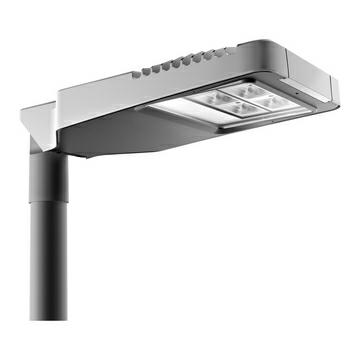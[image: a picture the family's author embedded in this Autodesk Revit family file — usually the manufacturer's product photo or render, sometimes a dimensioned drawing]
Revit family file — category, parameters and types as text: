
# Revit family: Lighting-StreetLighting-GEWISS-ROAD[5]MEDIUM-LED_OPTIC_WIDE_CLI
name_source: partatom
category: Apparecchi per illuminazione
units: mm (PartAtom-declared; Revit-internal decimal feet)

## family parameters
Basato su piano di lavoro = No
Condiviso = No
Punto di calcolo locali = No
Quota connettore circolare = Usa diametro
Sempre verticale = Sì
Sorgente d'illuminazione = No
Taglio con vuoti quando caricato = No
Tipo di parte = Normale

## types (49) — shared parameters
Applicazione = External
Catalogue = LIGHTING
IDF = 8ec06289-ca8c-48b1-8ae5-436b6d1e9ba1
IDT = c439c4f296dc4bdaaede42b4d003d5bb
IP degree = IP66
Immagine tipo = GWR5276M.jpg
Insulation class = I
Lampada = LED
Produttore = GEWISS S.p.A.
SEO = Street lighting
Shock resistance = IK08
Technical sheet = https://www.gewiss.com
URL = https://www.gewiss.com
Version file RFA = 20.11
Warranty = 5 years

## per-type parameters (varying)
- GWR5715M - ROAD5 MEDI WIDE 5M 4000K ,085A CL1 1-10V: Catalogue Range=ROAD [5]; Colour temperature=4000 K (CRI 70); Colour temperature:=4000 K (CRI 70); Descrizione=ROAD 5 MED.DIM.5M 4000K 0,85A O.W CL.I; EAN code=8011564873155; Electrocod=244C; LED LifeTime (L80B05)=120000H; LED current.=0,85A; Lamp-=LED; Lumen output (lm)=17090; Maximum surface exposed to the wind=0,19M2; Minimum distance from the illuminated object=1M; Modello=GWR5715M; No. Chorus modules=5 (5x3 LED); Nominal flux (lm)=21230; Number of modules=5 (5x3 LED); Operating temperature:=-25 +40 °C; Optic=W - ULOR: 0%; Overvoltage resistance=12 KV (Common and dfferential mode); Pilot current=0,85A; Power supply operation=Dimmable; System power=159W; Tilt adjustable=-20° ÷ +10° side bracket - -10° ÷ +20° pole head; Tipo alimentatore=Constant Current Driver Led; Tipologia=Dimmable; Voltage-=220/240 V - 50/60 Hz - Dimmable 1-10 V; Weight (kg)=8,8; Weight (kg):=8,8; Working temperature=-25 +40 °C
- GWR5775 - ROAD 5 MED.S.AL.5M 4000K 700mA O.W CL.I: Catalogue Range=ROAD [5]; Colour temperature=4000 K (CRI 70); Colour temperature:=4000 K (CRI 70); Descrizione=ROAD 5 MED.S.AL.5M 4000K 700mA O.W CL.I; EAN code=8011564873421; Electrocod=244C; LED LifeTime (L80B05)=77000H; LED current.=0,7A; Lamp-=LED; Lumen output (lm)=13100; Maximum surface exposed to the wind=0,19M2; Minimum distance from the illuminated object=1M; Modello=GWR5775; No. Chorus modules=5 (5x3 LED); Nominal flux (lm)=15600; Number of modules=5 (5x3 LED); Operating temperature:=-25 +50 °C; Optic=W - ULOR: 0%; Overvoltage resistance=12 KV (Common and dfferential mode); Pilot current=0,7A; System power=132W; Tilt adjustable=-20° ÷ +10° side bracket - -10° ÷ +20° pole head; Tipo alimentatore=Constant Current Driver Led; Tipologia=Stand alone; Voltage-=220/240 V - 50/60 Hz - Stand alone; Weight (kg)=8,8; Weight (kg):=8,8; Working temperature=-25 +50 °C
- GWR5773 - ROAD5 MEDI WIDE 3M 4000K 0,7A CL1: Catalogue Range=ROAD [5]; Colour temperature=4000 K (CRI 70); Colour temperature:=4000 K (CRI 70); Descrizione=ROAD 5 MED.S.AL.3M 4000K 700mA O.W CL.I; EAN code=8011564873360; Electrocod=244C; LED LifeTime (L80B05)=77000H; LED current.=0,7A; Lamp-=LED; Lumen output (lm)=7860; Maximum surface exposed to the wind=0,19M2; Minimum distance from the illuminated object=1M; Modello=GWR5773; No. Chorus modules=3 (3x3 LED); Nominal flux (lm)=9360; Number of modules=3 (3x3 LED); Operating temperature:=-25 +50 °C; Optic=W - ULOR: 0%; Overvoltage resistance=12 KV (Common and dfferential mode); Pilot current=0,7A; System power=79W; Tilt adjustable=-20° ÷ +10° side bracket - -10° ÷ +20° pole head; Tipo alimentatore=Constant Current Driver Led; Tipologia=Stand alone; Voltage-=220/240 V - 50/60 Hz - Stand alone; Weight (kg)=8; Weight (kg):=8; Working temperature=-25 +50 °C
- GWR5714M30K - ROAD5 MEDI WIDE 4M 3000K 1,0A CL1 1-10V: Body=Die-cast aluminium -; Catalogue Range=ROAD [5]; Classification:=-; Color Rendering Index=CRI-70; Colore=Graphite grey; Colour :=Powder coating; Colour temperature=3000K; Colour temperature:=3000 K (CRI>80); Context=Street and parking lighting; Control System=Dimmable 1-10 V; DIN 18032-3 certification=-; Descrizione=GWR5714M30K - ROAD5 MEDI WIDE 4M 3000K 1,0A CL1 1-10V; Device with reduced surface temperature=-; Driver=Included; Driver Box=Built-in; Efficiency (lm/W)=97; Electrocod=244C; Eletrical and lighting features=-; External screw=Stainless steel; Fixing=Pole Head - Outreach; Gasket=Anti-aging silicone; General information=-; Glow Wire Test :=-; IPEA=ROAD = B // LARGE AREAS = A ++ // CYCLOPEDONALS = B // GREEN AREAS = B // HISTORICAL CENTER = A3 +; Installationa and maintenance=-; LED Life Time (L80B05)=120000H; LED Maintenance=Not available; LED current.=1A; Lamp-=LED; Lifetime=L90B10 (Tq+25°C) = 100.000 h - L90B10 (Tq+40°C) = 50.000 h; Locking Hook=Integrated front handle; Lumen output (lm)=14800; Luminaire=LED Road Equipment; Materials=-; Maximum surface exposed to the wind=0,19M2; Maximum surface exposed to the wind :=0.19 m2; Minimum distance from the illuminated object=1M; Modello=GWR5714M30K; Mouting and installation=Pole Head - Outreach; Nominal flux (lm)=16560; Number of modules=4 (4x3 LED); Operating temperature :=-25 +40 °C; Operating temperature:=-25 +40 °C; Optic=WIDE; Optic :=Metallized polycarbonate reflector; Optic Maintenance=Not available; Optic and illuminating features=-; Overvoltage protection=DM 10KV / CM 10KV; Overvoltage resistance :=Common and dfferential mode: 10KV; Photobiological Risk Class=RG0; Power supply operation=Dimmable; Rated frequency (Hz)=50 / 60; Shield type=4mm thick flat tempered glass; Standard Deviation Colour Matching=SDCM = 5; Standard-=EN 60598-2-3, EN 60598-1 IEC/TR 62778; Standards and approvals=-; Stocking temperature=-; Supply voltage=220 - 240 V; System power=113W; System power :=153 W @ 1A; Tilt adjustable=-20° ÷ +10° side bracket - -10° ÷ +20° pole head; Tilt-=-20° ÷ +10° side bracket - -10° ÷ +20° pole head; Tipo alimentatore=Constant Current Driver Led; Tipologia=Dimmable; Type of light source=LED - Not replaceable; Unified Glare Rating=G*3 - ULOR = 0; Unique digital code (Datamatrix)=Currently not present; Voltage-=220/240 V - 50/60 Hz - Dimmable 1-10 V; Weight (kg):=8,4; Wiring=Isolating switch
- GWR5774B30K - ROAD5 MEDI WIDE 4M 3000K 0,7A CL1 BIREG: Body=Die-cast aluminium -; Catalogue Range=ROAD [5]; Classification:=-; Color Rendering Index=CRI-70; Colore=Graphite grey; Colour :=Powder coating; Colour temperature=3000K; Colour temperature:=3000 K (CRI>80); Context=Street and parking lighting; Control System=Bi-power with self-learning; DIN 18032-3 certification=-; Descrizione=GWR5774B30K - ROAD5 MEDI WIDE 4M 3000K 0,7A CL1 BIREG; Device with reduced surface temperature=-; Driver=Included; Driver Box=Built-in; Efficiency (lm/W)=102; Electrocod=244C; Eletrical and lighting features=-; External screw=Stainless steel; Fixing=Pole Head - Outreach; Gasket=Anti-aging silicone; General information=-; Glow Wire Test :=-; IPEA=ROAD = A + // LARGE AREAS = A3 + // CYCLOPEDONALS = A // GREEN AREAS = A // HISTORICAL CENTER = A4 +; Installationa and maintenance=-; LED Life Time (L80B05)=77000H; LED Maintenance=Not available; LED current.=0,7A; Lamp-=LED; Lifetime=L90B10 (Tq+25°C) = 100.000 h - L90B10 (Tq+50°C) = 50.000 h; Locking Hook=Integrated front handle; Lumen output (lm)=11000; Luminaire=LED Road Equipment; Materials=-; Maximum surface exposed to the wind=0,19M2; Maximum surface exposed to the wind :=0.19 m2; Minimum distance from the illuminated object=1M; Modello=GWR5774B30K; Mouting and installation=Pole Head - Outreach; Nominal flux (lm)=10800; Number of modules=4 (4x3 LED); Operating temperature :=-25 +50 °C; Operating temperature:=-25 +50 °C; Optic=WIDE; Optic :=Metallized polycarbonate reflector; Optic Maintenance=Not available; Optic and illuminating features=-; Overvoltage protection=DM 10KV / CM 10KV; Overvoltage resistance :=Common and dfferential mode: 10KV; Photobiological Risk Class=RG0; Power supply operation=Bi power; Rated frequency (Hz)=50 / 60; Shield type=4mm thick flat tempered glass; Standard Deviation Colour Matching=SDCM = 5; Standard-=EN 60598-2-3, EN 60598-1 IEC/TR 62778; Standards and approvals=-; Stocking temperature=-; Supply voltage=220 - 240 V; System power=108W; System power :=108 W @ 0.7A; Tilt adjustable=-20° ÷ +10° side bracket - -10° ÷ +20° pole head; Tilt-=-20° ÷ +10° side bracket - -10° ÷ +20° pole head; Tipo alimentatore=Constant Current Driver Led; Tipologia=Bi power; Type of light source=LED - Not replaceable; Unified Glare Rating=G*3 - ULOR = 0; Unique digital code (Datamatrix)=Currently not present; Voltage-=220/240 V - 50/60 Hz - Bi-power with self-learning; Weight (kg):=8,4; Wiring=Isolating switch
- GWR571630K - ROAD5 MEDI WIDE 6M 3000K 0,85A CL1: Body=Die-cast aluminium -; Catalogue Range=ROAD [5]; Classification:=-; Color Rendering Index=CRI-70; Colore=Graphite grey; Colour :=Powder coating; Colour temperature=3000K; Colour temperature:=3000 K (CRI>80); Context=Street and parking lighting; Control System=Stand alone; DIN 18032-3 certification=-; Descrizione=GWR571630K - ROAD5 MEDI WIDE 6M 3000K 0,85A CL1; Device with reduced surface temperature=-; Driver=Included; Driver Box=Built-in; Efficiency (lm/W)=105; Electrocod=244C; Eletrical and lighting features=-; External screw=Stainless steel; Fixing=Pole Head - Outreach; Gasket=Anti-aging silicone; General information=-; Glow Wire Test :=-; IPEA=ROAD = B // LARGE AREAS = A ++ // CYCLOPEDONALS = A // GREEN AREAS = A // HISTORICAL CENTER = A3 +; Installationa and maintenance=-; LED Life Time (L80B05)=120000H; LED Maintenance=Not available; LED current.=0,849999999999999A; Lamp-=LED; Lifetime=L90B10 (Tq+25°C) = 100.000 h - L90B10 (Tq+40°C) = 50.000 h; Locking Hook=Integrated front handle; Lumen output (lm)=19400; Luminaire=LED Road Equipment; Materials=-; Maximum surface exposed to the wind=0,19M2; Maximum surface exposed to the wind :=0.19 m2; Minimum distance from the illuminated object=1M; Modello=GWR571630K; Mouting and installation=Pole Head - Outreach; Nominal flux (lm)=21114; Number of modules=6 (6x3 LED); Operating temperature :=-25 +40 °C; Operating temperature:=-25 +40 °C; Optic=WIDE; Optic :=Metallized polycarbonate reflector; Optic Maintenance=Not available; Optic and illuminating features=-; Overvoltage protection=DM 10KV / CM 10KV; Overvoltage resistance :=Common and dfferential mode: 10KV; Photobiological Risk Class=RG0; Rated frequency (Hz)=50 / 60; Shield type=4mm thick flat tempered glass; Standard Deviation Colour Matching=SDCM = 5; Standard-=EN 60598-2-3, EN 60598-1 IEC/TR 62778; Standards and approvals=-; Stocking temperature=-; Supply voltage=220 - 240 V; System power=185W; System power :=185 W @ 0.85A; Tilt adjustable=-20° ÷ +10° side bracket - -10° ÷ +20° pole head; Tilt-=-20° ÷ +10° side bracket - -10° ÷ +20° pole head; Tipo alimentatore=Constant Current Driver Led; Tipologia=Stand alone; Type of light source=LED - Not replaceable; Unified Glare Rating=G*3 - ULOR = 0; Unique digital code (Datamatrix)=Currently not present; Voltage-=220/240 V - 50/60 Hz - Stand alone; Weight (kg):=9,09999999999999; Wiring=Isolating switch
- GWR5776 - ROAD5 MEDI WIDE 6M 4000K 0,7A CL1: Catalogue Range=ROAD [5]; Colour temperature=4000 K (CRI 70); Colour temperature:=4000 K (CRI 70); Descrizione=ROAD 5 MED.S.AL.6M 4000K 700mA O.W CL.I; EAN code=8011564873452; Electrocod=244C; LED LifeTime (L80B05)=77000H; LED current.=0,7A; Lamp-=LED; Lumen output (lm)=15730; Maximum surface exposed to the wind=0,19M2; Minimum distance from the illuminated object=1M; Modello=GWR5776; No. Chorus modules=6 (6x3 LED); Nominal flux (lm)=18720; Number of modules=6 (6x3 LED); Operating temperature:=-25 +50 °C; Optic=W - ULOR: 0%; Overvoltage resistance=12 KV (Common and dfferential mode); Pilot current=0,7A; System power=159W; Tilt adjustable=-20° ÷ +10° side bracket - -10° ÷ +20° pole head; Tipo alimentatore=Constant Current Driver Led; Tipologia=Stand alone; Voltage-=220/240 V - 50/60 Hz - Stand alone; Weight (kg)=9.1; Weight (kg):=9,1; Working temperature=-25 +50 °C
- GWR5776B30K - ROAD5 MEDI WIDE 6M 3000K 0,7A CL1 BIREG: Body=Die-cast aluminium -; Catalogue Range=ROAD [5]; Classification:=-; Color Rendering Index=CRI-70; Colore=Graphite grey; Colour :=Powder coating; Colour temperature=3000K; Colour temperature:=3000 K (CRI>80); Context=Street and parking lighting; Control System=Bi-power with self-learning; DIN 18032-3 certification=-; Descrizione=GWR5776B30K - ROAD5 MEDI WIDE 6M 3000K 0,7A CL1 BIREG; Device with reduced surface temperature=-; Driver=Included; Driver Box=Built-in; Efficiency (lm/W)=102; Electrocod=244C; Eletrical and lighting features=-; External screw=Stainless steel; Fixing=Pole Head - Outreach; Gasket=Anti-aging silicone; General information=-; Glow Wire Test :=-; IPEA=ROAD = A // LARGE AREAS = A3 + // CYCLOPEDONALS = A // GREEN AREAS = A // HISTORICAL CENTER = A4 +; Installationa and maintenance=-; LED Life Time (L80B05)=77000H; LED Maintenance=Not available; LED current.=0,7A; Lamp-=LED; Lifetime=L90B10 (Tq+25°C) = 100.000 h - L90B10 (Tq+50°C) = 50.000 h; Locking Hook=Integrated front handle; Lumen output (lm)=16500; Luminaire=LED Road Equipment; Materials=-; Maximum surface exposed to the wind=0,19M2; Maximum surface exposed to the wind :=0.19 m2; Minimum distance from the illuminated object=1M; Modello=GWR5776B30K; Mouting and installation=Pole Head - Outreach; Nominal flux (lm)=16200; Number of modules=6 (6x3 LED); Operating temperature :=-25 +50 °C; Operating temperature:=-25 +50 °C; Optic=WIDE; Optic :=Metallized polycarbonate reflector; Optic Maintenance=Not available; Optic and illuminating features=-; Overvoltage protection=DM 10KV / CM 10KV; Overvoltage resistance :=Common and dfferential mode: 10KV; Photobiological Risk Class=RG0; Power supply operation=Bi power; Rated frequency (Hz)=50 / 60; Shield type=4mm thick flat tempered glass; Standard Deviation Colour Matching=SDCM = 5; Standard-=EN 60598-2-3, EN 60598-1 IEC/TR 62778; Standards and approvals=-; Stocking temperature=-; Supply voltage=220 - 240 V; System power=161W; System power :=161 W @ 0.7A; Tilt adjustable=-20° ÷ +10° side bracket - -10° ÷ +20° pole head; Tilt-=-20° ÷ +10° side bracket - -10° ÷ +20° pole head; Tipo alimentatore=Constant Current Driver Led; Tipologia=Bi power; Type of light source=LED - Not replaceable; Unified Glare Rating=G*3 - ULOR = 0; Unique digital code (Datamatrix)=Currently not present; Voltage-=220/240 V - 50/60 Hz - Bi-power with self-learning; Weight (kg):=9,09999999999999; Wiring=Isolating switch
- GWR5776M - ROAD5 MEDI WIDE 6M 4000K 0,7A CL1 1-10V: Catalogue Range=ROAD [5]; Colour temperature=4000 K (CRI 70); Colour temperature:=4000 K (CRI 70); Descrizione=ROAD 5 MED.DIM.6M 4000K 700mA O.W CL.I; EAN code=8011564873476; Electrocod=244C; LED LifeTime (L80B05)=77000H; LED current.=0,7A; Lamp-=LED; Lumen output (lm)=15730; Maximum surface exposed to the wind=0,19M2; Minimum distance from the illuminated object=1M; Modello=GWR5776M; No. Chorus modules=6 (6x3 LED); Nominal flux (lm)=18720; Number of modules=6 (6x3 LED); Operating temperature:=-25 +50 °C; Optic=W - ULOR: 0%; Overvoltage resistance=12 KV (Common and dfferential mode); Pilot current=0,7A; Power supply operation=Dimmable; System power=159W; Tilt adjustable=-20° ÷ +10° side bracket - -10° ÷ +20° pole head; Tipo alimentatore=Constant Current Driver Led; Tipologia=Dimmable; Voltage-=220/240 V - 50/60 Hz - Dimmable 1-10 V; Weight (kg)=9.1; Weight (kg):=9,1; Working temperature=-25 +50 °C
- GWR5775M - ROAD5 MEDI WIDE 5M 4000K 0,7A CL1 1-10V: Catalogue Range=ROAD [5]; Colour temperature=4000 K (CRI 70); Colour temperature:=4000 K (CRI 70); Descrizione=ROAD 5 MED.DIM.5M 4000K 700mA O.W CL.I; EAN code=8011564873445; Electrocod=244C; LED LifeTime (L80B05)=77000H; LED current.=0,7A; Lamp-=LED; Lumen output (lm)=13100; Maximum surface exposed to the wind=0,19M2; Minimum distance from the illuminated object=1M; Modello=GWR5775M; No. Chorus modules=5 (5x3 LED); Nominal flux (lm)=15600; Number of modules=5 (5x3 LED); Operating temperature:=-25 +50 °C; Optic=W - ULOR: 0%; Overvoltage resistance=12 KV (Common and dfferential mode); Pilot current=0,7A; Power supply operation=Dimmable; System power=132W; Tilt adjustable=-20° ÷ +10° side bracket - -10° ÷ +20° pole head; Tipo alimentatore=Constant Current Driver Led; Tipologia=Dimmable; Voltage-=220/240 V - 50/60 Hz - Dimmable 1-10 V; Weight (kg)=8,8; Weight (kg):=8,8; Working temperature=-25 +50 °C
- GWR5773B - ROAD5 MEDI WIDE 3M 4000K 0,7A CL1 BIREG: Catalogue Range=ROAD [5]; Colour temperature=4000 K (CRI 70); Colour temperature:=4000 K (CRI 70); Descrizione=ROAD 5 MED.BI-PO.3M 4000K 700mA O.W CL.I; EAN code=8011564873377; Electrocod=244C; LED LifeTime (L80B05)=77000H; LED current.=0,7A; Lamp-=LED; Lumen output (lm)=7860; Maximum surface exposed to the wind=0,19M2; Minimum distance from the illuminated object=1M; Modello=GWR5773B; No. Chorus modules=3 (3x3 LED); Nominal flux (lm)=9360; Number of modules=3 (3x3 LED); Operating temperature:=-25 +50 °C; Optic=W - ULOR: 0%; Overvoltage resistance=12 KV (Common and dfferential mode); Pilot current=0,7A; Power supply operation=Bi power; System power=81W; Tilt adjustable=-20° ÷ +10° side bracket - -10° ÷ +20° pole head; Tipo alimentatore=Constant Current Driver Led; Tipologia=Bi power; Voltage-=220/240 V - 50/60 Hz - Bi-power with self-learning; Weight (kg)=8; Weight (kg):=8; Working temperature=-25 +50 °C
- GWR5713M - ROAD5 MEDI WIDE 3M 4000K 1,0A CL1 1-10V: Catalogue Range=ROAD [5]; Colour temperature=4000 K (CRI 70); Colour temperature:=4000 K (CRI 70); Descrizione=ROAD 5 MED.DIM.3M 4000K 1A O.W CL.I; EAN code=8011564873094; Electrocod=244C; LED LifeTime (L80B05)=120000H; LED current.=1A; Lamp-=LED; Lumen output (lm)=11520; Maximum surface exposed to the wind=0,19M2; Minimum distance from the illuminated object=1M; Modello=GWR5713M; No. Chorus modules=3 (3x3 LED); Nominal flux (lm)=14310; Number of modules=3 (3x3 LED); Operating temperature:=-25 +40 °C; Optic=W - ULOR: 0%; Overvoltage resistance=12 KV (Common and dfferential mode); Pilot current=1A; Power supply operation=Dimmable; System power=113W; Tilt adjustable=-20° ÷ +10° side bracket - -10° ÷ +20° pole head; Tipo alimentatore=Constant Current Driver Led; Tipologia=Dimmable; Voltage-=220/240 V - 50/60 Hz - Dimmable 1-10 V; Weight (kg)=8; Weight (kg):=8; Working temperature=-25 +40 °C
- GWR5716B - ROAD5 MEDI WIDE 6M 4000K 0,85A CL1 BIREG: Catalogue Range=ROAD [5]; Colour temperature=4000 K (CRI 70); Colour temperature:=4000 K (CRI 70); Descrizione=ROAD5 MED.BI-POW.6M 4000K 0,85A O.W CL.I; EAN code=8011564873179; Electrocod=244C; LED LifeTime (L80B05)=120000H; LED current.=0,85A; Lamp-=LED; Lumen output (lm)=19580; Maximum surface exposed to the wind=0,19M2; Minimum distance from the illuminated object=1M; Modello=GWR5716B; No. Chorus modules=6 (6x3 LED); Nominal flux (lm)=24330; Number of modules=6 (6x3 LED); Operating temperature:=-25 +40 °C; Optic=W - ULOR: 0%; Overvoltage resistance=12 KV (Common and dfferential mode); Pilot current=0,85A; Power supply operation=Bi power; System power=187W; Tilt adjustable=-20° ÷ +10° side bracket - -10° ÷ +20° pole head; Tipo alimentatore=Constant Current Driver Led; Tipologia=Bi power; Voltage-=220/240 V - 50/60 Hz - Bi-power with self-learning; Weight (kg)=9.1; Weight (kg):=9,1; Working temperature=-25 +40 °C
- GWR5714 - ROAD 5 MED.S.AL.4M 4000K 1A O.W CL.I: Catalogue Range=ROAD [5]; Colour temperature=4000 K (CRI 70); Colour temperature:=4000 K (CRI 70); Descrizione=ROAD 5 MED.S.AL.4M 4000K 1A O.W CL.I; EAN code=8011564873100; Electrocod=244C; LED LifeTime (L80B05)=120000H; LED current.=1A; Lamp-=LED; Lumen output (lm)=15360; Maximum surface exposed to the wind=0,19M2; Minimum distance from the illuminated object=1M; Modello=GWR5714; No. Chorus modules=4 (4x3 LED); Nominal flux (lm)=19080; Number of modules=4 (4x3 LED); Operating temperature:=-25 +40 °C; Optic=W - ULOR: 0%; Overvoltage resistance=12 KV (Common and dfferential mode); Pilot current=1A; System power=151W; Tilt adjustable=-20° ÷ +10° side bracket - -10° ÷ +20° pole head; Tipo alimentatore=Constant Current Driver Led; Tipologia=Stand alone; Voltage-=220/240 V - 50/60 Hz - Stand alone; Weight (kg)=8,4; Weight (kg):=8,4; Working temperature=-25 +40 °C
- GWR5715 - ROAD 5 MED.S.AL.5M 4000K 0,85A O.W CL.I: Catalogue Range=ROAD [5]; Colour temperature=4000 K (CRI 70); Colour temperature:=4000 K (CRI 70); Descrizione=ROAD 5 MED.S.AL.5M 4000K 0,85A O.W CL.I; EAN code=8011564873131; Electrocod=244C; LED LifeTime (L80B05)=120000H; LED current.=0,85A; Lamp-=LED; Lumen output (lm)=17090; Maximum surface exposed to the wind=0,19M2; Minimum distance from the illuminated object=1M; Modello=GWR5715; No. Chorus modules=5 (5x3 LED); Nominal flux (lm)=21230; Number of modules=5 (5x3 LED); Operating temperature:=-25 +40 °C; Optic=W - ULOR: 0%; Overvoltage resistance=12 KV (Common and dfferential mode); Pilot current=0,85A; System power=159W; Tilt adjustable=-20° ÷ +10° side bracket - -10° ÷ +20° pole head; Tipo alimentatore=Constant Current Driver Led; Tipologia=Stand alone; Voltage-=220/240 V - 50/60 Hz - Stand alone; Weight (kg)=8,8; Weight (kg):=8,8; Working temperature=-25 +40 °C
- GWR571330K - ROAD5 MEDI WIDE 3M 3000K 1,0A CL1: Body=Die-cast aluminium -; Catalogue Range=ROAD [5]; Classification:=-; Color Rendering Index=CRI-70; Colore=Graphite grey; Colour :=Powder coating; Colour temperature=3000K; Colour temperature:=3000 K (CRI>80); Context=Street and parking lighting; Control System=Stand alone; DIN 18032-3 certification=-; Descrizione=GWR571330K - ROAD5 MEDI WIDE 3M 3000K 1,0A CL1; Device with reduced surface temperature=-; Driver=Included; Driver Box=Built-in; Efficiency (lm/W)=98; Electrocod=244C; Eletrical and lighting features=-; External screw=Stainless steel; Fixing=Pole Head - Outreach; Gasket=Anti-aging silicone; General information=-; Glow Wire Test :=-; IPEA=ROAD = A // LARGE AREAS = A3 + // CYCLOPEDONALS = A // GREEN AREAS = A // HISTORICAL CENTER = A4 +; Installationa and maintenance=-; LED Life Time (L80B05)=120000H; LED Maintenance=Not available; LED current.=1A; Lamp-=LED; Lifetime=L90B10 (Tq+25°C) = 100.000 h - L90B10 (Tq+40°C) = 75.000 h; Locking Hook=Integrated front handle; Lumen output (lm)=11100; Luminaire=LED Road Equipment; Materials=-; Maximum surface exposed to the wind=0,19M2; Maximum surface exposed to the wind :=0.19 m2; Minimum distance from the illuminated object=1M; Modello=GWR571330K; Mouting and installation=Pole Head - Outreach; Nominal flux (lm)=12420; Number of modules=3 (3x3 LED); Operating temperature :=-25 +40 °C; Operating temperature:=-25 +40 °C; Optic=WIDE; Optic :=Metallized polycarbonate reflector; Optic Maintenance=Not available; Optic and illuminating features=-; Overvoltage protection=DM 10KV / CM 10KV; Overvoltage resistance :=Common and dfferential mode: 10KV; Photobiological Risk Class=RG0; Rated frequency (Hz)=50 / 60; Shield type=4mm thick flat tempered glass; Standard Deviation Colour Matching=SDCM = 5; Standard-=EN 60598-2-3, EN 60598-1 IEC/TR 62778; Standards and approvals=-; Stocking temperature=-; Supply voltage=220 - 240 V; System power=113W; System power :=113 W @ 1A; Tilt adjustable=-20° ÷ +10° side bracket - -10° ÷ +20° pole head; Tilt-=-20° ÷ +10° side bracket - -10° ÷ +20° pole head; Tipo alimentatore=Constant Current Driver Led; Tipologia=Stand alone; Type of light source=LED - Not replaceable; Unified Glare Rating=G*3 - ULOR = 0; Unique digital code (Datamatrix)=Currently not present; Voltage-=220/240 V - 50/60 Hz - Stand alone; Weight (kg):=8; Wiring=Isolating switch
- GWR5713V - ROAD5 MEDI V.WIDE 3M 4000K 1,0A CL1: Body=Die-cast aluminium -; Classification:=-; Color Rendering Index=CRI-70; Colore=Graphite grey; Colour :=Powder coating; Colour temperature=4000K; Context=Street and parking lighting; Control System=DALI; DIN 18032-3 certification=-; Descrizione=GWR5713V - ROAD5 MEDI V.WIDE 3M 4000K 1,0A CL1; Device with reduced surface temperature=-; Driver=Included; Driver Box=Built-in; Efficiency (lm/W)=111; Eletrical and lighting features=-; External screw=Stainless steel; Fixing=Pole Head - Outreach; Gasket=Anti-aging silicone; General information=-; Glow Wire Test :=-; IPEA=ROAD = A ++ // LARGE AREAS = A4 + // CYCLOPEDONALS = A ++ // GREEN AREAS = A ++ // HISTORICAL CENTER = A6 +; Installationa and maintenance=-; LED Maintenance=Not available; Lifetime=L90B10 (Tq+25°C) = 100.000 h - L90B10 (Tq+40°C) = 75.000 h; Locking Hook=Integrated front handle; Lumen output (lm)=12800; Luminaire=LED Road Equipment; Materials=-; Maximum surface exposed to the wind :=0.19 m2; Modello=GWR5713V; Mouting and installation=Pole Head - Outreach; Number of modules=3 (3x3 LED); Operating temperature :=-25 +40 °C; Optic=WIDE; Optic :=Metallized polycarbonate reflector; Optic Maintenance=Not available; Optic and illuminating features=-; Overvoltage protection=DM 10KV / CM 10KV; Photobiological Risk Class=RG0; Rated frequency (Hz)=50 / 60; Shield type=4mm thick flat tempered glass; Standard Deviation Colour Matching=SDCM = 5; Standard-=EN 60598-2-3, EN 60598-1 IEC/TR 62778; Standards and approvals=-; Stocking temperature=-; Supply voltage=220 - 240 V; System power :=115 W @ 1A; Tilt-=-20° ÷ +10° side bracket - -10° ÷ +20° pole head; Type of light source=LED - Not replaceable; Unified Glare Rating=G*3 - ULOR = 0; Unique digital code (Datamatrix)=Currently not present; Weight (kg):=8; Wiring=Isolating switch
- GWR5716M30K - ROAD5 MEDI WIDE 6M 3000K 0,85A CL1 1-10V: Body=Die-cast aluminium -; Catalogue Range=ROAD [5]; Classification:=-; Color Rendering Index=CRI-70; Colore=Graphite grey; Colour :=Powder coating; Colour temperature=3000K; Colour temperature:=3000 K (CRI>80); Context=Street and parking lighting; Control System=Dimmable 1-10 V; DIN 18032-3 certification=-; Descrizione=GWR5716M30K - ROAD5 MEDI WIDE 6M 3000K 0,85A CL1 1-10V; Device with reduced surface temperature=-; Driver=Included; Driver Box=Built-in; Efficiency (lm/W)=104; Electrocod=244C; Eletrical and lighting features=-; External screw=Stainless steel; Fixing=Pole Head - Outreach; Gasket=Anti-aging silicone; General information=-; Glow Wire Test :=-; IPEA=ROAD = B // LARGE AREAS = A ++ // CYCLOPEDONALS = A // GREEN AREAS = A // HISTORICAL CENTER = A3 +; Installationa and maintenance=-; LED Life Time (L80B05)=120000H; LED Maintenance=Not available; LED current.=0,849999999999999A; Lamp-=LED; Lifetime=L90B10 (Tq+25°C) = 100.000 h - L90B10 (Tq+40°C) = 50.000 h; Locking Hook=Integrated front handle; Lumen output (lm)=19400; Luminaire=LED Road Equipment; Materials=-; Maximum surface exposed to the wind=0,19M2; Maximum surface exposed to the wind :=0.19 m2; Minimum distance from the illuminated object=1M; Modello=GWR5716M30K; Mouting and installation=Pole Head - Outreach; Nominal flux (lm)=21114; Number of modules=6 (6x3 LED); Operating temperature :=-25 +40 °C; Operating temperature:=-25 +40 °C; Optic=WIDE; Optic :=Metallized polycarbonate reflector; Optic Maintenance=Not available; Optic and illuminating features=-; Overvoltage protection=DM 10KV / CM 10KV; Overvoltage resistance :=Common and dfferential mode: 10KV; Photobiological Risk Class=RG0; Power supply operation=Dimmable; Rated frequency (Hz)=50 / 60; Shield type=4mm thick flat tempered glass; Standard Deviation Colour Matching=SDCM = 5; Standard-=EN 60598-2-3, EN 60598-1 IEC/TR 62778; Standards and approvals=-; Stocking temperature=-; Supply voltage=220 - 240 V; System power=185W; System power :=187 W @ 0.85A; Tilt adjustable=-20° ÷ +10° side bracket - -10° ÷ +20° pole head; Tilt-=-20° ÷ +10° side bracket - -10° ÷ +20° pole head; Tipo alimentatore=Constant Current Driver Led; Tipologia=Dimmable; Type of light source=LED - Not replaceable; Unified Glare Rating=G*3 - ULOR = 0; Unique digital code (Datamatrix)=Currently not present; Voltage-=220/240 V - 50/60 Hz - Dimmable 1-10 V; Weight (kg):=9,09999999999999; Wiring=Isolating switch
- GWR577630K - ROAD5 MEDI WIDE 6M 3000K 0,7A CL1: Body=Die-cast aluminium -; Catalogue Range=ROAD [5]; Classification:=-; Color Rendering Index=CRI-70; Colore=Graphite grey; Colour :=Powder coating; Colour temperature=3000K; Colour temperature:=3000 K (CRI>80); Context=Street and parking lighting; Control System=Stand alone; DIN 18032-3 certification=-; Descrizione=GWR577630K - ROAD5 MEDI WIDE 6M 3000K 0,7A CL1; Device with reduced surface temperature=-; Driver=Included; Driver Box=Built-in; Efficiency (lm/W)=104; Electrocod=244C; Eletrical and lighting features=-; External screw=Stainless steel; Fixing=Pole Head - Outreach; Gasket=Anti-aging silicone; General information=-; Glow Wire Test :=-; IPEA=ROAD = A // LARGE AREAS = A3 + // CYCLOPEDONALS = A // GREEN AREAS = A // HISTORICAL CENTER = A4 +; Installationa and maintenance=-; LED Life Time (L80B05)=77000H; LED Maintenance=Not available; LED current.=0,7A; Lamp-=LED; Lifetime=L90B10 (Tq+25°C) = 100.000 h - L90B10 (Tq+50°C) = 50.000 h; Locking Hook=Integrated front handle; Lumen output (lm)=16500; Luminaire=LED Road Equipment; Materials=-; Maximum surface exposed to the wind=0,19M2; Maximum surface exposed to the wind :=0.19 m2; Minimum distance from the illuminated object=1M; Modello=GWR577630K; Mouting and installation=Pole Head - Outreach; Nominal flux (lm)=16200; Number of modules=6 (6x3 LED); Operating temperature :=-25 +50 °C; Operating temperature:=-25 +50 °C; Optic=WIDE; Optic :=Metallized polycarbonate reflector; Optic Maintenance=Not available; Optic and illuminating features=-; Overvoltage protection=DM 10KV / CM 10KV; Overvoltage resistance :=Common and dfferential mode: 10KV; Photobiological Risk Class=RG0; Rated frequency (Hz)=50 / 60; Shield type=4mm thick flat tempered glass; Standard Deviation Colour Matching=SDCM = 5; Standard-=EN 60598-2-3, EN 60598-1 IEC/TR 62778; Standards and approvals=-; Stocking temperature=-; Supply voltage=220 - 240 V; System power=159W; System power :=159 W @ 0.7A; Tilt adjustable=-20° ÷ +10° side bracket - -10° ÷ +20° pole head; Tilt-=-20° ÷ +10° side bracket - -10° ÷ +20° pole head; Tipo alimentatore=Constant Current Driver Led; Tipologia=Stand alone; Type of light source=LED - Not replaceable; Unified Glare Rating=G*3 - ULOR = 0; Unique digital code (Datamatrix)=Currently not present; Voltage-=220/240 V - 50/60 Hz - Stand alone; Weight (kg):=9,09999999999999; Wiring=Isolating switch
- GWR571530K - ROAD5 MEDI WIDE 5M 3000K 0,85A CL1: Body=Die-cast aluminium -; Catalogue Range=ROAD [5]; Classification:=-; Color Rendering Index=CRI-70; Colore=Graphite grey; Colour :=Powder coating; Colour temperature=3000K; Colour temperature:=3000 K (CRI>80); Context=Street and parking lighting; Control System=Stand alone; DIN 18032-3 certification=-; Descrizione=GWR571530K - ROAD5 MEDI WIDE 5M 3000K 0,85A CL1; Device with reduced surface temperature=-; Driver=Included; Driver Box=Built-in; Efficiency (lm/W)=102; Electrocod=244C; Eletrical and lighting features=-; External screw=Stainless steel; Fixing=Pole Head - Outreach; Gasket=Anti-aging silicone; General information=-; Glow Wire Test :=-; IPEA=ROAD = A // LARGE AREAS = A3 + // CYCLOPEDONALS = A // GREEN AREAS = A // HISTORICAL CENTER = A4 +; Installationa and maintenance=-; LED Life Time (L80B05)=120000H; LED Maintenance=Not available; LED current.=0,849999999999999A; Lamp-=LED; Lifetime=L90B10 (Tq+25°C) = 100.000 h - L90B10 (Tq+40°C) = 50.000 h; Locking Hook=Integrated front handle; Lumen output (lm)=16200; Luminaire=LED Road Equipment; Materials=-; Maximum surface exposed to the wind=0,19M2; Maximum surface exposed to the wind :=0.19 m2; Minimum distance from the illuminated object=1M; Modello=GWR571530K; Mouting and installation=Pole Head - Outreach; Nominal flux (lm)=18423; Number of modules=5 (5x3 LED); Operating temperature :=-25 +40 °C; Operating temperature:=-25 +40 °C; Optic=WIDE; Optic :=Metallized polycarbonate reflector; Optic Maintenance=Not available; Optic and illuminating features=-; Overvoltage protection=DM 10KV / CM 10KV; Overvoltage resistance :=Common and dfferential mode: 10KV; Photobiological Risk Class=RG0; Rated frequency (Hz)=50 / 60; Shield type=4mm thick flat tempered glass; Standard Deviation Colour Matching=SDCM = 5; Standard-=EN 60598-2-3, EN 60598-1 IEC/TR 62778; Standards and approvals=-; Stocking temperature=-; Supply voltage=220 - 240 V; System power=159W; System power :=159 W @ 0.85A; Tilt adjustable=-20° ÷ +10° side bracket - -10° ÷ +20° pole head; Tilt-=-20° ÷ +10° side bracket - -10° ÷ +20° pole head; Tipo alimentatore=Constant Current Driver Led; Tipologia=Stand alone; Type of light source=LED - Not replaceable; Unified Glare Rating=G*3 - ULOR = 0; Unique digital code (Datamatrix)=Currently not present; Voltage-=220/240 V - 50/60 Hz - Stand alone; Weight (kg):=8,8; Wiring=Isolating switch
- GWR5773M30K - ROAD5 MEDI WIDE 3M 3000K 0,7A CL1 1-10V: Body=Die-cast aluminium -; Catalogue Range=ROAD [5]; Classification:=-; Color Rendering Index=CRI-70; Colore=Graphite grey; Colour :=Powder coating; Colour temperature=3000K; Colour temperature:=3000 K (CRI>80); Context=Street and parking lighting; Control System=Dimmable 1-10 V; DIN 18032-3 certification=-; Descrizione=GWR5773M30K - ROAD5 MEDI WIDE 3M 3000K 0,7A CL1 1-10V; Device with reduced surface temperature=-; Driver=Included; Driver Box=Built-in; Efficiency (lm/W)=102; Electrocod=244C; Eletrical and lighting features=-; External screw=Stainless steel; Fixing=Pole Head - Outreach; Gasket=Anti-aging silicone; General information=-; Glow Wire Test :=-; IPEA=ROAD = A ++ // LARGE AREAS = A3 + // CYCLOPEDONALS = A + // GREEN AREAS = A + // HISTORICAL CENTER = A6 +; Installationa and maintenance=-; LED Life Time (L80B05)=77000H; LED Maintenance=Not available; LED current.=0,7A; Lamp-=LED; Lifetime=L90B10 (Tq+25°C) = 100.000 h - L90B10 (Tq+50°C) = 75.000 h; Locking Hook=Integrated front handle; Lumen output (lm)=8300; Luminaire=LED Road Equipment; Materials=-; Maximum surface exposed to the wind=0,19M2; Maximum surface exposed to the wind :=0.19 m2; Minimum distance from the illuminated object=1M; Modello=GWR5773M30K; Mouting and installation=Pole Head - Outreach; Nominal flux (lm)=8100; Number of modules=3 (3x3 LED); Operating temperature :=-25 +50 °C; Operating temperature:=-25 +50 °C; Optic=WIDE; Optic :=Metallized polycarbonate reflector; Optic Maintenance=Not available; Optic and illuminating features=-; Overvoltage protection=DM 10KV / CM 10KV; Overvoltage resistance :=Common and dfferential mode: 10KV; Photobiological Risk Class=RG0; Power supply operation=Dimmable; Rated frequency (Hz)=50 / 60; Shield type=4mm thick flat tempered glass; Standard Deviation Colour Matching=SDCM = 5; Standard-=EN 60598-2-3, EN 60598-1 IEC/TR 62778; Standards and approvals=-; Stocking temperature=-; Supply voltage=220 - 240 V; System power=79W; System power :=81 W @ 0.7A; Tilt adjustable=-20° ÷ +10° side bracket - -10° ÷ +20° pole head; Tilt-=-20° ÷ +10° side bracket - -10° ÷ +20° pole head; Tipo alimentatore=Constant Current Driver Led; Tipologia=Dimmable; Type of light source=LED - Not replaceable; Unified Glare Rating=G*3 - ULOR = 0; Unique digital code (Datamatrix)=Currently not present; Voltage-=220/240 V - 50/60 Hz - Dimmable 1-10 V; Weight (kg):=8; Wiring=Isolating switch
- GWR5713B30K - ROAD5 MEDI WIDE 3M 3000K 1,0A CL1 BIREG: Body=Die-cast aluminium -; Catalogue Range=ROAD [5]; Classification:=-; Color Rendering Index=CRI-70; Colore=Graphite grey; Colour :=Powder coating; Colour temperature=3000K; Colour temperature:=3000 K (CRI>80); Context=Street and parking lighting; Control System=Bi-power with self-learning; DIN 18032-3 certification=-; Descrizione=GWR5713B30K - ROAD5 MEDI WIDE 3M 3000K 1,0A CL1 BIREG; Device with reduced surface temperature=-; Driver=Included; Driver Box=Built-in; Efficiency (lm/W)=97; Electrocod=244C; Eletrical and lighting features=-; External screw=Stainless steel; Fixing=Pole Head - Outreach; Gasket=Anti-aging silicone; General information=-; Glow Wire Test :=-; IPEA=ROAD = A // LARGE AREAS = A ++ // CYCLOPEDONALS = A // GREEN AREAS = A // HISTORICAL CENTER = A3 +; Installationa and maintenance=-; LED Life Time (L80B05)=120000H; LED Maintenance=Not available; LED current.=1A; Lamp-=LED; Lifetime=L90B10 (Tq+25°C) = 100.000 h - L90B10 (Tq+40°C) = 75.000 h; Locking Hook=Integrated front handle; Lumen output (lm)=11100; Luminaire=LED Road Equipment; Materials=-; Maximum surface exposed to the wind=0,19M2; Maximum surface exposed to the wind :=0.19 m2; Minimum distance from the illuminated object=1M; Modello=GWR5713B30K; Mouting and installation=Pole Head - Outreach; Nominal flux (lm)=12420; Number of modules=3 (3x3 LED); Operating temperature :=-25 +40 °C; Operating temperature:=-25 +40 °C; Optic=WIDE; Optic :=Metallized polycarbonate reflector; Optic Maintenance=Not available; Optic and illuminating features=-; Overvoltage protection=DM 10KV / CM 10KV; Overvoltage resistance :=Common and dfferential mode: 10KV; Photobiological Risk Class=RG0; Power supply operation=Bi power; Rated frequency (Hz)=50 / 60; Shield type=4mm thick flat tempered glass; Standard Deviation Colour Matching=SDCM = 5; Standard-=EN 60598-2-3, EN 60598-1 IEC/TR 62778; Standards and approvals=-; Stocking temperature=-; Supply voltage=220 - 240 V; System power=115W; System power :=115 W @ 1A; Tilt adjustable=-20° ÷ +10° side bracket - -10° ÷ +20° pole head; Tilt-=-20° ÷ +10° side bracket - -10° ÷ +20° pole head; Tipo alimentatore=Constant Current Driver Led; Tipologia=Bi power; Type of light source=LED - Not replaceable; Unified Glare Rating=G*3 - ULOR = 0; Unique digital code (Datamatrix)=Currently not present; Voltage-=220/240 V - 50/60 Hz - Bi-power with self-learning; Weight (kg):=8; Wiring=Isolating switch
- GWR571430K - ROAD5 MEDI WIDE 4M 3000K 1,0A CL1: Body=Die-cast aluminium -; Catalogue Range=ROAD [5]; Classification:=-; Color Rendering Index=CRI-70; Colore=Graphite grey; Colour :=Powder coating; Colour temperature=3000K; Colour temperature:=3000 K (CRI>80); Context=Street and parking lighting; Control System=Stand alone; DIN 18032-3 certification=-; Descrizione=GWR571430K - ROAD5 MEDI WIDE 4M 3000K 1,0A CL1; Device with reduced surface temperature=-; Driver=Included; Driver Box=Built-in; Efficiency (lm/W)=98; Electrocod=244C; Eletrical and lighting features=-; External screw=Stainless steel; Fixing=Pole Head - Outreach; Gasket=Anti-aging silicone; General information=-; Glow Wire Test :=-; IPEA=ROAD = B // LARGE AREAS = A ++ // CYCLOPEDONALS = A // GREEN AREAS = A // HISTORICAL CENTER = A4 +; Installationa and maintenance=-; LED Life Time (L80B05)=120000H; LED Maintenance=Not available; LED current.=1A; Lamp-=LED; Lifetime=L90B10 (Tq+25°C) = 100.000 h - L90B10 (Tq+40°C) = 50.000 h; Locking Hook=Integrated front handle; Lumen output (lm)=14800; Luminaire=LED Road Equipment; Materials=-; Maximum surface exposed to the wind=0,19M2; Maximum surface exposed to the wind :=0.19 m2; Minimum distance from the illuminated object=1M; Modello=GWR571430K; Mouting and installation=Pole Head - Outreach; Nominal flux (lm)=16560; Number of modules=4 (4x3 LED); Operating temperature :=-25 +40 °C; Operating temperature:=-25 +40 °C; Optic=WIDE; Optic :=Metallized polycarbonate reflector; Optic Maintenance=Not available; Optic and illuminating features=-; Overvoltage protection=DM 10KV / CM 10KV; Overvoltage resistance :=Common and dfferential mode: 10KV; Photobiological Risk Class=RG0; Rated frequency (Hz)=50 / 60; Shield type=4mm thick flat tempered glass; Standard Deviation Colour Matching=SDCM = 5; Standard-=EN 60598-2-3, EN 60598-1 IEC/TR 62778; Standards and approvals=-; Stocking temperature=-; Supply voltage=220 - 240 V; System power=151W; System power :=151 W @ 1A; Tilt adjustable=-20° ÷ +10° side bracket - -10° ÷ +20° pole head; Tilt-=-20° ÷ +10° side bracket - -10° ÷ +20° pole head; Tipo alimentatore=Constant Current Driver Led; Tipologia=Stand alone; Type of light source=LED - Not replaceable; Unified Glare Rating=G*3 - ULOR = 0; Unique digital code (Datamatrix)=Currently not present; Voltage-=220/240 V - 50/60 Hz - Stand alone; Weight (kg):=8,4; Wiring=Isolating switch
- GWR5715B30K - ROAD5 MEDI WIDE 5M 3000K 0,85A CL1 BIREG: Body=Die-cast aluminium -; Catalogue Range=ROAD [5]; Classification:=-; Color Rendering Index=CRI-70; Colore=Graphite grey; Colour :=Powder coating; Colour temperature=3000K; Colour temperature:=3000 K (CRI>80); Context=Street and parking lighting; Control System=Bi-power with self-learning; DIN 18032-3 certification=-; Descrizione=GWR5715B30K - ROAD5 MEDI WIDE 5M 3000K 0,85A CL1 BIREG; Device with reduced surface temperature=-; Driver=Included; Driver Box=Built-in; Efficiency (lm/W)=101; Electrocod=244C; Eletrical and lighting features=-; External screw=Stainless steel; Fixing=Pole Head - Outreach; Gasket=Anti-aging silicone; General information=-; Glow Wire Test :=-; IPEA=ROAD = A // LARGE AREAS = A ++ // CYCLOPEDONALS = A // GREEN AREAS = A // HISTORICAL CENTER = A4 +; Installationa and maintenance=-; LED Life Time (L80B05)=120000H; LED Maintenance=Not available; LED current.=0,849999999999999A; Lamp-=LED; Lifetime=L90B10 (Tq+25°C) = 100.000 h - L90B10 (Tq+40°C) = 50.000 h; Locking Hook=Integrated front handle; Lumen output (lm)=16200; Luminaire=LED Road Equipment; Materials=-; Maximum surface exposed to the wind=0,19M2; Maximum surface exposed to the wind :=0.19 m2; Minimum distance from the illuminated object=1M; Modello=GWR5715B30K; Mouting and installation=Pole Head - Outreach; Nominal flux (lm)=18423; Number of modules=5 (5x3 LED); Operating temperature :=-25 +40 °C; Operating temperature:=-25 +40 °C; Optic=WIDE; Optic :=Metallized polycarbonate reflector; Optic Maintenance=Not available; Optic and illuminating features=-; Overvoltage protection=DM 10KV / CM 10KV; Overvoltage resistance :=Common and dfferential mode: 10KV; Photobiological Risk Class=RG0; Power supply operation=Bi power; Rated frequency (Hz)=50 / 60; Shield type=4mm thick flat tempered glass; Standard Deviation Colour Matching=SDCM = 5; Standard-=EN 60598-2-3, EN 60598-1 IEC/TR 62778; Standards and approvals=-; Stocking temperature=-; Supply voltage=220 - 240 V; System power=161W; System power :=161 W @ 0.85A; Tilt adjustable=-20° ÷ +10° side bracket - -10° ÷ +20° pole head; Tilt-=-20° ÷ +10° side bracket - -10° ÷ +20° pole head; Tipo alimentatore=Constant Current Driver Led; Tipologia=Bi power; Type of light source=LED - Not replaceable; Unified Glare Rating=G*3 - ULOR = 0; Unique digital code (Datamatrix)=Currently not present; Voltage-=220/240 V - 50/60 Hz - Bi-power with self-learning; Weight (kg):=8,8; Wiring=Isolating switch
- GWR577430K - ROAD5 MEDI WIDE 4M 3000K 0,7A CL1: Body=Die-cast aluminium -; Catalogue Range=ROAD [5]; Classification:=-; Color Rendering Index=CRI-70; Colore=Graphite grey; Colour :=Powder coating; Colour temperature=3000K; Colour temperature:=3000 K (CRI>80); Context=Street and parking lighting; Control System=Stand alone; DIN 18032-3 certification=-; Descrizione=GWR577430K - ROAD5 MEDI WIDE 4M 3000K 0,7A CL1; Device with reduced surface temperature=-; Driver=Included; Driver Box=Built-in; Efficiency (lm/W)=104; Electrocod=244C; Eletrical and lighting features=-; External screw=Stainless steel; Fixing=Pole Head - Outreach; Gasket=Anti-aging silicone; General information=-; Glow Wire Test :=-; IPEA=ROAD = A + // LARGE AREAS = A3 + // CYCLOPEDONALS = A + // GREEN AREAS = A + // HISTORICAL CENTER = A4 +; Installationa and maintenance=-; LED Life Time (L80B05)=77000H; LED Maintenance=Not available; LED current.=0,7A; Lamp-=LED; Lifetime=L90B10 (Tq+25°C) = 100.000 h - L90B10 (Tq+50°C) = 50.000 h; Locking Hook=Integrated front handle; Lumen output (lm)=11000; Luminaire=LED Road Equipment; Materials=-; Maximum surface exposed to the wind=0,19M2; Maximum surface exposed to the wind :=0.19 m2; Minimum distance from the illuminated object=1M; Modello=GWR577430K; Mouting and installation=Pole Head - Outreach; Nominal flux (lm)=10800; Number of modules=4 (4x3 LED); Operating temperature :=-25 +50 °C; Operating temperature:=-25 +50 °C; Optic=WIDE; Optic :=Metallized polycarbonate reflector; Optic Maintenance=Not available; Optic and illuminating features=-; Overvoltage protection=DM 10KV / CM 10KV; Overvoltage resistance :=Common and dfferential mode: 10KV; Photobiological Risk Class=RG0; Rated frequency (Hz)=50 / 60; Shield type=4mm thick flat tempered glass; Standard Deviation Colour Matching=SDCM = 5; Standard-=EN 60598-2-3, EN 60598-1 IEC/TR 62778; Standards and approvals=-; Stocking temperature=-; Supply voltage=220 - 240 V; System power=106W; System power :=106 W @ 0.7A; Tilt adjustable=-20° ÷ +10° side bracket - -10° ÷ +20° pole head; Tilt-=-20° ÷ +10° side bracket - -10° ÷ +20° pole head; Tipo alimentatore=Constant Current Driver Led; Tipologia=Stand alone; Type of light source=LED - Not replaceable; Unified Glare Rating=G*3 - ULOR = 0; Unique digital code (Datamatrix)=Currently not present; Voltage-=220/240 V - 50/60 Hz - Stand alone; Weight (kg):=8,4; Wiring=Isolating switch
- GWR5776B - ROAD5 MEDI WIDE 6M 4000K 0,7A CL1 BIREG: Catalogue Range=ROAD [5]; Colour temperature=4000 K (CRI 70); Colour temperature:=4000 K (CRI 70); Descrizione=ROAD 5 MED.BI-PO.6M 4000K 700mA O.W CL.I; EAN code=8011564873469; Electrocod=244C; LED LifeTime (L80B05)=77000H; LED current.=0,7A; Lamp-=LED; Lumen output (lm)=15730; Maximum surface exposed to the wind=0,19M2; Minimum distance from the illuminated object=1M; Modello=GWR5776B; No. Chorus modules=6 (6x3 LED); Nominal flux (lm)=18720; Number of modules=6 (6x3 LED); Operating temperature:=-25 +50 °C; Optic=W - ULOR: 0%; Overvoltage resistance=12 KV (Common and dfferential mode); Pilot current=0,7A; Power supply operation=Bi power; System power=161W; Tilt adjustable=-20° ÷ +10° side bracket - -10° ÷ +20° pole head; Tipo alimentatore=Constant Current Driver Led; Tipologia=Bi power; Voltage-=220/240 V - 50/60 Hz - Bi-power with self-learning; Weight (kg)=9.1; Weight (kg):=9,1; Working temperature=-25 +50 °C
- GWR5713M30K - ROAD5 MEDI WIDE 3M 3000K 1,0A CL1 1-10V: Body=Die-cast aluminium -; Catalogue Range=ROAD [5]; Classification:=-; Color Rendering Index=CRI-70; Colore=Graphite grey; Colour :=Powder coating; Colour temperature=3000K; Colour temperature:=3000 K (CRI>80); Context=Street and parking lighting; Control System=Dimmable 1-10 V; DIN 18032-3 certification=-; Descrizione=GWR5713M30K - ROAD5 MEDI WIDE 3M 3000K 1,0A CL1 1-10V; Device with reduced surface temperature=-; Driver=Included; Driver Box=Built-in; Efficiency (lm/W)=97; Electrocod=244C; Eletrical and lighting features=-; External screw=Stainless steel; Fixing=Pole Head - Outreach; Gasket=Anti-aging silicone; General information=-; Glow Wire Test :=-; IPEA=ROAD = A // LARGE AREAS = A ++ // CYCLOPEDONALS = A // GREEN AREAS = A // HISTORICAL CENTER = A3 +; Installationa and maintenance=-; LED Life Time (L80B05)=120000H; LED Maintenance=Not available; LED current.=1A; Lamp-=LED; Lifetime=L90B10 (Tq+25°C) = 100.000 h - L90B10 (Tq+40°C) = 75.000 h; Locking Hook=Integrated front handle; Lumen output (lm)=11100; Luminaire=LED Road Equipment; Materials=-; Maximum surface exposed to the wind=0,19M2; Maximum surface exposed to the wind :=0.19 m2; Minimum distance from the illuminated object=1M; Modello=GWR5713M30K; Mouting and installation=Pole Head - Outreach; Nominal flux (lm)=12420; Number of modules=3 (3x3 LED); Operating temperature :=-25 +40 °C; Operating temperature:=-25 +40 °C; Optic=WIDE; Optic :=Metallized polycarbonate reflector; Optic Maintenance=Not available; Optic and illuminating features=-; Overvoltage protection=DM 10KV / CM 10KV; Overvoltage resistance :=Common and dfferential mode: 10KV; Photobiological Risk Class=RG0; Power supply operation=Dimmable; Rated frequency (Hz)=50 / 60; Shield type=4mm thick flat tempered glass; Standard Deviation Colour Matching=SDCM = 5; Standard-=EN 60598-2-3, EN 60598-1 IEC/TR 62778; Standards and approvals=-; Stocking temperature=-; Supply voltage=220 - 240 V; System power=113W; System power :=115 W @ 1A; Tilt adjustable=-20° ÷ +10° side bracket - -10° ÷ +20° pole head; Tilt-=-20° ÷ +10° side bracket - -10° ÷ +20° pole head; Tipo alimentatore=Constant Current Driver Led; Tipologia=Dimmable; Type of light source=LED - Not replaceable; Unified Glare Rating=G*3 - ULOR = 0; Unique digital code (Datamatrix)=Currently not present; Voltage-=220/240 V - 50/60 Hz - Dimmable 1-10 V; Weight (kg):=8; Wiring=Isolating switch
- GWR5716B30K - ROAD5 MEDI WIDE 6M 3000K 0,85A CL1 BIREG: Body=Die-cast aluminium -; Catalogue Range=ROAD [5]; Classification:=-; Color Rendering Index=CRI-70; Colore=Graphite grey; Colour :=Powder coating; Colour temperature=3000K; Colour temperature:=3000 K (CRI>80); Context=Street and parking lighting; Control System=Bi-power with self-learning; DIN 18032-3 certification=-; Descrizione=GWR5716B30K - ROAD5 MEDI WIDE 6M 3000K 0,85A CL1 BIREG; Device with reduced surface temperature=-; Driver=Included; Driver Box=Built-in; Efficiency (lm/W)=104; Electrocod=244C; Eletrical and lighting features=-; External screw=Stainless steel; Fixing=Pole Head - Outreach; Gasket=Anti-aging silicone; General information=-; Glow Wire Test :=-; IPEA=ROAD = B // LARGE AREAS = A ++ // CYCLOPEDONALS = A // GREEN AREAS = A // HISTORICAL CENTER = A3 +; Installationa and maintenance=-; LED Life Time (L80B05)=120000H; LED Maintenance=Not available; LED current.=0,849999999999999A; Lamp-=LED; Lifetime=L90B10 (Tq+25°C) = 100.000 h - L90B10 (Tq+40°C) = 50.000 h; Locking Hook=Integrated front handle; Lumen output (lm)=19400; Luminaire=LED Road Equipment; Materials=-; Maximum surface exposed to the wind=0,19M2; Maximum surface exposed to the wind :=0.19 m2; Minimum distance from the illuminated object=1M; Modello=GWR5716B30K; Mouting and installation=Pole Head - Outreach; Nominal flux (lm)=21114; Number of modules=6 (6x3 LED); Operating temperature :=-25 +40 °C; Operating temperature:=-25 +40 °C; Optic=WIDE; Optic :=Metallized polycarbonate reflector; Optic Maintenance=Not available; Optic and illuminating features=-; Overvoltage protection=DM 10KV / CM 10KV; Overvoltage resistance :=Common and dfferential mode: 10KV; Photobiological Risk Class=RG0; Power supply operation=Bi power; Rated frequency (Hz)=50 / 60; Shield type=4mm thick flat tempered glass; Standard Deviation Colour Matching=SDCM = 5; Standard-=EN 60598-2-3, EN 60598-1 IEC/TR 62778; Standards and approvals=-; Stocking temperature=-; Supply voltage=220 - 240 V; System power=187W; System power :=187 W @ 0.85A; Tilt adjustable=-20° ÷ +10° side bracket - -10° ÷ +20° pole head; Tilt-=-20° ÷ +10° side bracket - -10° ÷ +20° pole head; Tipo alimentatore=Constant Current Driver Led; Tipologia=Bi power; Type of light source=LED - Not replaceable; Unified Glare Rating=G*3 - ULOR = 0; Unique digital code (Datamatrix)=Currently not present; Voltage-=220/240 V - 50/60 Hz - Bi-power with self-learning; Weight (kg):=9,09999999999999; Wiring=Isolating switch
- GWR5714B30K - ROAD5 MEDI WIDE 4M 3000K 1,0A CL1 BIREG: Body=Die-cast aluminium -; Catalogue Range=ROAD [5]; Classification:=-; Color Rendering Index=CRI-70; Colore=Graphite grey; Colour :=Powder coating; Colour temperature=3000K; Colour temperature:=3000 K (CRI>80); Context=Street and parking lighting; Control System=Bi-power with self-learning; DIN 18032-3 certification=-; Descrizione=GWR5714B30K - ROAD5 MEDI WIDE 4M 3000K 1,0A CL1 BIREG; Device with reduced surface temperature=-; Driver=Included; Driver Box=Built-in; Efficiency (lm/W)=97; Electrocod=244C; Eletrical and lighting features=-; External screw=Stainless steel; Fixing=Pole Head - Outreach; Gasket=Anti-aging silicone; General information=-; Glow Wire Test :=-; IPEA=ROAD = B // LARGE AREAS = A ++ // CYCLOPEDONALS = B // GREEN AREAS = B // HISTORICAL CENTER = A3 +; Installationa and maintenance=-; LED Life Time (L80B05)=120000H; LED Maintenance=Not available; LED current.=1A; Lamp-=LED; Lifetime=L90B10 (Tq+25°C) = 100.000 h - L90B10 (Tq+40°C) = 50.000 h; Locking Hook=Integrated front handle; Lumen output (lm)=14800; Luminaire=LED Road Equipment; Materials=-; Maximum surface exposed to the wind=0,19M2; Maximum surface exposed to the wind :=0.19 m2; Minimum distance from the illuminated object=1M; Modello=GWR5714B30K; Mouting and installation=Pole Head - Outreach; Nominal flux (lm)=16560; Number of modules=4 (4x3 LED); Operating temperature :=-25 +40 °C; Operating temperature:=-25 +40 °C; Optic=WIDE; Optic :=Metallized polycarbonate reflector; Optic Maintenance=Not available; Optic and illuminating features=-; Overvoltage protection=DM 10KV / CM 10KV; Overvoltage resistance :=Common and dfferential mode: 10KV; Photobiological Risk Class=RG0; Power supply operation=Bi power; Rated frequency (Hz)=50 / 60; Shield type=4mm thick flat tempered glass; Standard Deviation Colour Matching=SDCM = 5; Standard-=EN 60598-2-3, EN 60598-1 IEC/TR 62778; Standards and approvals=-; Stocking temperature=-; Supply voltage=220 - 240 V; System power=153W; System power :=153 W @ 1A; Tilt adjustable=-20° ÷ +10° side bracket - -10° ÷ +20° pole head; Tilt-=-20° ÷ +10° side bracket - -10° ÷ +20° pole head; Tipo alimentatore=Constant Current Driver Led; Tipologia=Bi power; Type of light source=LED - Not replaceable; Unified Glare Rating=G*3 - ULOR = 0; Unique digital code (Datamatrix)=Currently not present; Voltage-=220/240 V - 50/60 Hz - Bi-power with self-learning; Weight (kg):=8,4; Wiring=Isolating switch
- GWR5716 - ROAD 5 MED.S.AL.6M 4000K 0,85A O.W CL.I: Catalogue Range=ROAD [5]; Colour temperature=4000 K (CRI 70); Colour temperature:=4000 K (CRI 70); Descrizione=ROAD 5 MED.S.AL.6M 4000K 0,85A O.W CL.I; EAN code=8011564873162; Electrocod=244C; LED LifeTime (L80B05)=120000H; LED current.=0,85A; Lamp-=LED; Lumen output (lm)=19580; Maximum surface exposed to the wind=0,19M2; Minimum distance from the illuminated object=1M; Modello=GWR5716; No. Chorus modules=6 (6x3 LED); Nominal flux (lm)=24330; Number of modules=6 (6x3 LED); Operating temperature:=-25 +40 °C; Optic=W - ULOR: 0%; Overvoltage resistance=12 KV (Common and dfferential mode); Pilot current=0,85A; System power=185W; Tilt adjustable=-20° ÷ +10° side bracket - -10° ÷ +20° pole head; Tipo alimentatore=Constant Current Driver Led; Tipologia=Stand alone; Voltage-=220/240 V - 50/60 Hz - Stand alone; Weight (kg)=9.1; Weight (kg):=9,1; Working temperature=-25 +40 °C
- GWR5773B30K - ROAD5 MEDI WIDE 3M 3000K 0,7A CL1 BIREG: Body=Die-cast aluminium -; Catalogue Range=ROAD [5]; Classification:=-; Color Rendering Index=CRI-70; Colore=Graphite grey; Colour :=Powder coating; Colour temperature=3000K; Colour temperature:=3000 K (CRI>80); Context=Street and parking lighting; Control System=Bi-power with self-learning; DIN 18032-3 certification=-; Descrizione=GWR5773B30K - ROAD5 MEDI WIDE 3M 3000K 0,7A CL1 BIREG; Device with reduced surface temperature=-; Driver=Included; Driver Box=Built-in; Efficiency (lm/W)=102; Electrocod=244C; Eletrical and lighting features=-; External screw=Stainless steel; Fixing=Pole Head - Outreach; Gasket=Anti-aging silicone; General information=-; Glow Wire Test :=-; IPEA=ROAD = A ++ // LARGE AREAS = A3 + // CYCLOPEDONALS = A + // GREEN AREAS = A + // HISTORICAL CENTER = A6 +; Installationa and maintenance=-; LED Life Time (L80B05)=77000H; LED Maintenance=Not available; LED current.=0,7A; Lamp-=LED; Lifetime=L90B10 (Tq+25°C) = 100.000 h - L90B10 (Tq+50°C) = 75.000 h; Locking Hook=Integrated front handle; Lumen output (lm)=8300; Luminaire=LED Road Equipment; Materials=-; Maximum surface exposed to the wind=0,19M2; Maximum surface exposed to the wind :=0.19 m2; Minimum distance from the illuminated object=1M; Modello=GWR5773B30K; Mouting and installation=Pole Head - Outreach; Nominal flux (lm)=8100; Number of modules=3 (3x3 LED); Operating temperature :=-25 +50 °C; Operating temperature:=-25 +50 °C; Optic=WIDE; Optic :=Metallized polycarbonate reflector; Optic Maintenance=Not available; Optic and illuminating features=-; Overvoltage protection=DM 10KV / CM 10KV; Overvoltage resistance :=Common and dfferential mode: 10KV; Photobiological Risk Class=RG0; Power supply operation=Bi power; Rated frequency (Hz)=50 / 60; Shield type=4mm thick flat tempered glass; Standard Deviation Colour Matching=SDCM = 5; Standard-=EN 60598-2-3, EN 60598-1 IEC/TR 62778; Standards and approvals=-; Stocking temperature=-; Supply voltage=220 - 240 V; System power=81W; System power :=81 W @ 0.7A; Tilt adjustable=-20° ÷ +10° side bracket - -10° ÷ +20° pole head; Tilt-=-20° ÷ +10° side bracket - -10° ÷ +20° pole head; Tipo alimentatore=Constant Current Driver Led; Tipologia=Bi power; Type of light source=LED - Not replaceable; Unified Glare Rating=G*3 - ULOR = 0; Unique digital code (Datamatrix)=Currently not present; Voltage-=220/240 V - 50/60 Hz - Bi-power with self-learning; Weight (kg):=8; Wiring=Isolating switch
- GWR5776M30K - ROAD5 MEDI WIDE 6M 3000K 0,7A CL1 1-10V: Body=Die-cast aluminium -; Catalogue Range=ROAD [5]; Classification:=-; Color Rendering Index=CRI-70; Colore=Graphite grey; Colour :=Powder coating; Colour temperature=3000K; Colour temperature:=3000 K (CRI>80); Context=Street and parking lighting; Control System=Dimmable 1-10 V; DIN 18032-3 certification=-; Descrizione=GWR5776M30K - ROAD5 MEDI WIDE 6M 3000K 0,7A CL1 1-10V; Device with reduced surface temperature=-; Driver=Included; Driver Box=Built-in; Efficiency (lm/W)=102; Electrocod=244C; Eletrical and lighting features=-; External screw=Stainless steel; Fixing=Pole Head - Outreach; Gasket=Anti-aging silicone; General information=-; Glow Wire Test :=-; IPEA=ROAD = A // LARGE AREAS = A3 + // CYCLOPEDONALS = A // GREEN AREAS = A // HISTORICAL CENTER = A4 +; Installationa and maintenance=-; LED Life Time (L80B05)=77000H; LED Maintenance=Not available; LED current.=0,7A; Lamp-=LED; Lifetime=L90B10 (Tq+25°C) = 100.000 h - L90B10 (Tq+50°C) = 50.000 h; Locking Hook=Integrated front handle; Lumen output (lm)=16500; Luminaire=LED Road Equipment; Materials=-; Maximum surface exposed to the wind=0,19M2; Maximum surface exposed to the wind :=0.19 m2; Minimum distance from the illuminated object=1M; Modello=GWR5776M30K; Mouting and installation=Pole Head - Outreach; Nominal flux (lm)=16200; Number of modules=6 (6x3 LED); Operating temperature :=-25 +50 °C; Operating temperature:=-25 +50 °C; Optic=WIDE; Optic :=Metallized polycarbonate reflector; Optic Maintenance=Not available; Optic and illuminating features=-; Overvoltage protection=DM 10KV / CM 10KV; Overvoltage resistance :=Common and dfferential mode: 10KV; Photobiological Risk Class=RG0; Power supply operation=Dimmable; Rated frequency (Hz)=50 / 60; Shield type=4mm thick flat tempered glass; Standard Deviation Colour Matching=SDCM = 5; Standard-=EN 60598-2-3, EN 60598-1 IEC/TR 62778; Standards and approvals=-; Stocking temperature=-; Supply voltage=220 - 240 V; System power=159W; System power :=161 W @ 0.7A; Tilt adjustable=-20° ÷ +10° side bracket - -10° ÷ +20° pole head; Tilt-=-20° ÷ +10° side bracket - -10° ÷ +20° pole head; Tipo alimentatore=Constant Current Driver Led; Tipologia=Dimmable; Type of light source=LED - Not replaceable; Unified Glare Rating=G*3 - ULOR = 0; Unique digital code (Datamatrix)=Currently not present; Voltage-=220/240 V - 50/60 Hz - Dimmable 1-10 V; Weight (kg):=9,09999999999999; Wiring=Isolating switch
- GWR5713B - ROAD5 MEDI WIDE 3M 4000K 1,0A CL1 BIREG: Catalogue Range=ROAD [5]; Colour temperature=4000 K (CRI 70); Colour temperature:=4000 K (CRI 70); Descrizione=ROAD 5 MED.BI-POW.3M 4000K 1A O.W CL.I; EAN code=8011564873087; Electrocod=244C; LED LifeTime (L80B05)=120000H; LED current.=1A; Lamp-=LED; Lumen output (lm)=11520; Maximum surface exposed to the wind=0,19M2; Minimum distance from the illuminated object=1M; Modello=GWR5713B; No. Chorus modules=3 (3x3 LED); Nominal flux (lm)=14310; Number of modules=3 (3x3 LED); Operating temperature:=-25 +40 °C; Optic=W - ULOR: 0%; Overvoltage resistance=12 KV (Common and dfferential mode); Pilot current=1A; Power supply operation=Bi power; System power=115W; Tilt adjustable=-20° ÷ +10° side bracket - -10° ÷ +20° pole head; Tipo alimentatore=Constant Current Driver Led; Tipologia=Bi power; Voltage-=220/240 V - 50/60 Hz - Bi-power with self-learning; Weight (kg)=8; Weight (kg):=8; Working temperature=-25 +40 °C
- GWR5774M - ROAD5 MEDI WIDE 4M 4000K 0,7A CL1 1-10V: Catalogue Range=ROAD [5]; Colour temperature=4000 K (CRI 70); Colour temperature:=4000 K (CRI 70); Descrizione=ROAD 5 MED.DIM.4M 4000K 700mA O.W CL.I; EAN code=8011564873414; Electrocod=244C; LED LifeTime (L80B05)=77000H; LED current.=0,7A; Lamp-=LED; Lumen output (lm)=10480; Maximum surface exposed to the wind=0,19M2; Minimum distance from the illuminated object=1M; Modello=GWR5774M; No. Chorus modules=4 (4x3 LED); Nominal flux (lm)=12480; Number of modules=4 (4x3 LED); Operating temperature:=-25 +50 °C; Optic=W - ULOR: 0%; Overvoltage resistance=12 KV (Common and dfferential mode); Pilot current=0,7A; Power supply operation=Dimmable; System power=106W; Tilt adjustable=-20° ÷ +10° side bracket - -10° ÷ +20° pole head; Tipo alimentatore=Constant Current Driver Led; Tipologia=Dimmable; Voltage-=220/240 V - 50/60 Hz - Dimmable 1-10 V; Weight (kg)=8,4; Weight (kg):=8,4; Working temperature=-25 +50 °C
- GWR5774M30K - ROAD5 MEDI WIDE 4M 3000K 0,7A CL1 1-10V: Body=Die-cast aluminium -; Catalogue Range=ROAD [5]; Classification:=-; Color Rendering Index=CRI-70; Colore=Graphite grey; Colour :=Powder coating; Colour temperature=3000K; Colour temperature:=3000 K (CRI>80); Context=Street and parking lighting; Control System=Dimmable 1-10 V; DIN 18032-3 certification=-; Descrizione=GWR5774M30K - ROAD5 MEDI WIDE 4M 3000K 0,7A CL1 1-10V; Device with reduced surface temperature=-; Driver=Included; Driver Box=Built-in; Efficiency (lm/W)=102; Electrocod=244C; Eletrical and lighting features=-; External screw=Stainless steel; Fixing=Pole Head - Outreach; Gasket=Anti-aging silicone; General information=-; Glow Wire Test :=-; IPEA=ROAD = A + // LARGE AREAS = A3 + // CYCLOPEDONALS = A // GREEN AREAS = A // HISTORICAL CENTER = A4 +; Installationa and maintenance=-; LED Life Time (L80B05)=77000H; LED Maintenance=Not available; LED current.=0,7A; Lamp-=LED; Lifetime=L90B10 (Tq+25°C) = 100.000 h - L90B10 (Tq+50°C) = 50.000 h; Locking Hook=Integrated front handle; Lumen output (lm)=11000; Luminaire=LED Road Equipment; Materials=-; Maximum surface exposed to the wind=0,19M2; Maximum surface exposed to the wind :=0.19 m2; Minimum distance from the illuminated object=1M; Modello=GWR5774M30K; Mouting and installation=Pole Head - Outreach; Nominal flux (lm)=10800; Number of modules=4 (4x3 LED); Operating temperature :=-25 +50 °C; Operating temperature:=-25 +50 °C; Optic=WIDE; Optic :=Metallized polycarbonate reflector; Optic Maintenance=Not available; Optic and illuminating features=-; Overvoltage protection=DM 10KV / CM 10KV; Overvoltage resistance :=Common and dfferential mode: 10KV; Photobiological Risk Class=RG0; Power supply operation=Dimmable; Rated frequency (Hz)=50 / 60; Shield type=4mm thick flat tempered glass; Standard Deviation Colour Matching=SDCM = 5; Standard-=EN 60598-2-3, EN 60598-1 IEC/TR 62778; Standards and approvals=-; Stocking temperature=-; Supply voltage=220 - 240 V; System power=106W; System power :=108 W @ 0.7A; Tilt adjustable=-20° ÷ +10° side bracket - -10° ÷ +20° pole head; Tilt-=-20° ÷ +10° side bracket - -10° ÷ +20° pole head; Tipo alimentatore=Constant Current Driver Led; Tipologia=Dimmable; Type of light source=LED - Not replaceable; Unified Glare Rating=G*3 - ULOR = 0; Unique digital code (Datamatrix)=Currently not present; Voltage-=220/240 V - 50/60 Hz - Dimmable 1-10 V; Weight (kg):=8,4; Wiring=Isolating switch
- GWR5774B - ROAD5 MEDI WIDE 4M 4000K 0,7A CL1 BIREG: Catalogue Range=ROAD [5]; Colour temperature=4000 K (CRI 70); Colour temperature:=4000 K (CRI 70); Descrizione=ROAD 5 MED.BI-PO.4M 4000K 700mA O.W CL.I; EAN code=8011564873407; Electrocod=244C; LED LifeTime (L80B05)=77000H; LED current.=0,7A; Lamp-=LED; Lumen output (lm)=10480; Maximum surface exposed to the wind=0,19M2; Minimum distance from the illuminated object=1M; Modello=GWR5774B; No. Chorus modules=4 (4x3 LED); Nominal flux (lm)=12480; Number of modules=4 (4x3 LED); Operating temperature:=-25 +50 °C; Optic=W - ULOR: 0%; Overvoltage resistance=12 KV (Common and dfferential mode); Pilot current=0,7A; Power supply operation=Bi power; System power=108W; Tilt adjustable=-20° ÷ +10° side bracket - -10° ÷ +20° pole head; Tipo alimentatore=Constant Current Driver Led; Tipologia=Bi power; Voltage-=220/240 V - 50/60 Hz - Bi-power with self-learning; Weight (kg)=8,4; Weight (kg):=8,4; Working temperature=-25 +50 °C
- GWR5715M30K - ROAD5 MEDI WIDE 5M 3000K 0,85A CL1 1-10V: Body=Die-cast aluminium -; Catalogue Range=ROAD [5]; Classification:=-; Color Rendering Index=CRI-70; Colore=Graphite grey; Colour :=Powder coating; Colour temperature=3000K; Colour temperature:=3000 K (CRI>80); Context=Street and parking lighting; Control System=Dimmable 1-10 V; DIN 18032-3 certification=-; Descrizione=GWR5715M30K - ROAD5 MEDI WIDE 5M 3000K 0,85A CL1 1-10V; Device with reduced surface temperature=-; Driver=Included; Driver Box=Built-in; Efficiency (lm/W)=101; Electrocod=244C; Eletrical and lighting features=-; External screw=Stainless steel; Fixing=Pole Head - Outreach; Gasket=Anti-aging silicone; General information=-; Glow Wire Test :=-; IPEA=ROAD = A // LARGE AREAS = A ++ // CYCLOPEDONALS = A // GREEN AREAS = A // HISTORICAL CENTER = A4 +; Installationa and maintenance=-; LED Life Time (L80B05)=120000H; LED Maintenance=Not available; LED current.=0,849999999999999A; Lamp-=LED; Lifetime=L90B10 (Tq+25°C) = 100.000 h - L90B10 (Tq+40°C) = 50.000 h; Locking Hook=Integrated front handle; Lumen output (lm)=16200; Luminaire=LED Road Equipment; Materials=-; Maximum surface exposed to the wind=0,19M2; Maximum surface exposed to the wind :=0.19 m2; Minimum distance from the illuminated object=1M; Modello=GWR5715M30K; Mouting and installation=Pole Head - Outreach; Nominal flux (lm)=18423; Number of modules=5 (5x3 LED); Operating temperature :=-25 +40 °C; Operating temperature:=-25 +40 °C; Optic=WIDE; Optic :=Metallized polycarbonate reflector; Optic Maintenance=Not available; Optic and illuminating features=-; Overvoltage protection=DM 10KV / CM 10KV; Overvoltage resistance :=Common and dfferential mode: 10KV; Photobiological Risk Class=RG0; Power supply operation=Dimmable; Rated frequency (Hz)=50 / 60; Shield type=4mm thick flat tempered glass; Standard Deviation Colour Matching=SDCM = 5; Standard-=EN 60598-2-3, EN 60598-1 IEC/TR 62778; Standards and approvals=-; Stocking temperature=-; Supply voltage=220 - 240 V; System power=159W; System power :=161 W @ 0.85A; Tilt adjustable=-20° ÷ +10° side bracket - -10° ÷ +20° pole head; Tilt-=-20° ÷ +10° side bracket - -10° ÷ +20° pole head; Tipo alimentatore=Constant Current Driver Led; Tipologia=Dimmable; Type of light source=LED - Not replaceable; Unified Glare Rating=G*3 - ULOR = 0; Unique digital code (Datamatrix)=Currently not present; Voltage-=220/240 V - 50/60 Hz - Dimmable 1-10 V; Weight (kg):=8,8; Wiring=Isolating switch
- GWR5716M - ROAD5 MEDI WIDE 6M 4000K 0,85A CL1 1-10V: Catalogue Range=ROAD [5]; Colour temperature=4000 K (CRI 70); Colour temperature:=4000 K (CRI 70); Descrizione=ROAD 5 MED.DIM.6M 4000K 0,85A O.W CL.I; EAN code=8011564873186; Electrocod=244C; LED LifeTime (L80B05)=120000H; LED current.=0,85A; Lamp-=LED; Lumen output (lm)=19580; Maximum surface exposed to the wind=0,19M2; Minimum distance from the illuminated object=1M; Modello=GWR5716M; No. Chorus modules=6 (6x3 LED); Nominal flux (lm)=24330; Number of modules=6 (6x3 LED); Operating temperature:=-25 +40 °C; Optic=W - ULOR: 0%; Overvoltage resistance=12 KV (Common and dfferential mode); Pilot current=0,85A; Power supply operation=Dimmable; System power=185W; Tilt adjustable=-20° ÷ +10° side bracket - -10° ÷ +20° pole head; Tipo alimentatore=Constant Current Driver Led; Tipologia=Dimmable; Voltage-=220/240 V - 50/60 Hz - Dimmable 1-10 V; Weight (kg)=9.1; Weight (kg):=9,1; Working temperature=-25 +40 °C
- GWR5775M30K - ROAD5 MEDI WIDE 5M 3000K 0,7A CL1 1-10V: Body=Die-cast aluminium -; Catalogue Range=ROAD [5]; Classification:=-; Color Rendering Index=CRI-70; Colore=Graphite grey; Colour :=Powder coating; Colour temperature=3000K; Colour temperature:=3000 K (CRI>80); Context=Street and parking lighting; Control System=Dimmable 1-10 V; DIN 18032-3 certification=-; Descrizione=GWR5775M30K - ROAD5 MEDI WIDE 5M 3000K 0,7A CL1 1-10V; Device with reduced surface temperature=-; Driver=Included; Driver Box=Built-in; Efficiency (lm/W)=102; Electrocod=244C; Eletrical and lighting features=-; External screw=Stainless steel; Fixing=Pole Head - Outreach; Gasket=Anti-aging silicone; General information=-; Glow Wire Test :=-; IPEA=ROAD = A // LARGE AREAS = A3 + // CYCLOPEDONALS = A // GREEN AREAS = A // HISTORICAL CENTER = A4 +; Installationa and maintenance=-; LED Life Time (L80B05)=77000H; LED Maintenance=Not available; LED current.=0,7A; Lamp-=LED; Lifetime=L90B10 (Tq+25°C) = 100.000 h - L90B10 (Tq+50°C) = 50.000 h; Locking Hook=Integrated front handle; Lumen output (lm)=13700; Luminaire=LED Road Equipment; Materials=-; Maximum surface exposed to the wind=0,19M2; Maximum surface exposed to the wind :=0.19 m2; Minimum distance from the illuminated object=1M; Modello=GWR5775M30K; Mouting and installation=Pole Head - Outreach; Nominal flux (lm)=13500; Number of modules=5 (5x3 LED); Operating temperature :=-25 +50 °C; Operating temperature:=-25 +50 °C; Optic=WIDE; Optic :=Metallized polycarbonate reflector; Optic Maintenance=Not available; Optic and illuminating features=-; Overvoltage protection=DM 10KV / CM 10KV; Overvoltage resistance :=Common and dfferential mode: 10KV; Photobiological Risk Class=RG0; Power supply operation=Dimmable; Rated frequency (Hz)=50 / 60; Shield type=4mm thick flat tempered glass; Standard Deviation Colour Matching=SDCM = 5; Standard-=EN 60598-2-3, EN 60598-1 IEC/TR 62778; Standards and approvals=-; Stocking temperature=-; Supply voltage=220 - 240 V; System power=132W; System power :=134 W @ 0.7A; Tilt adjustable=-20° ÷ +10° side bracket - -10° ÷ +20° pole head; Tilt-=-20° ÷ +10° side bracket - -10° ÷ +20° pole head; Tipo alimentatore=Constant Current Driver Led; Tipologia=Dimmable; Type of light source=LED - Not replaceable; Unified Glare Rating=G*3 - ULOR = 0; Unique digital code (Datamatrix)=Currently not present; Voltage-=220/240 V - 50/60 Hz - Dimmable 1-10 V; Weight (kg):=8,8; Wiring=Isolating switch
- GWR5715B - ROAD5 MEDI WIDE 5M 4000K 0,85A CL1 BIREG: Catalogue Range=ROAD [5]; Colour temperature=4000 K (CRI 70); Colour temperature:=4000 K (CRI 70); Descrizione=ROAD5 MED.BI-POW.5M 4000K 0,85A O.W CL.I; EAN code=8011564873148; Electrocod=244C; LED LifeTime (L80B05)=120000H; LED current.=0,85A; Lamp-=LED; Lumen output (lm)=17090; Maximum surface exposed to the wind=0,19M2; Minimum distance from the illuminated object=1M; Modello=GWR5715B; No. Chorus modules=5 (5x3 LED); Nominal flux (lm)=21230; Number of modules=5 (5x3 LED); Operating temperature:=-25 +40 °C; Optic=W - ULOR: 0%; Overvoltage resistance=12 KV (Common and dfferential mode); Pilot current=0,85A; Power supply operation=Bi power; System power=161W; Tilt adjustable=-20° ÷ +10° side bracket - -10° ÷ +20° pole head; Tipo alimentatore=Constant Current Driver Led; Tipologia=Bi power; Voltage-=220/240 V - 50/60 Hz - Bi-power with self-learning; Weight (kg)=8,8; Weight (kg):=8,8; Working temperature=-25 +40 °C
- GWR577330K - ROAD5 MEDI WIDE 3M 3000K 0,7A CL1: Body=Die-cast aluminium -; Catalogue Range=ROAD [5]; Classification:=-; Color Rendering Index=CRI-70; Colore=Graphite grey; Colour :=Powder coating; Colour temperature=3000K; Colour temperature:=3000 K (CRI>80); Context=Street and parking lighting; Control System=Stand alone; DIN 18032-3 certification=-; Descrizione=GWR577330K - ROAD5 MEDI WIDE 3M 3000K 0,7A CL1; Device with reduced surface temperature=-; Driver=Included; Driver Box=Built-in; Efficiency (lm/W)=105; Electrocod=244C; Eletrical and lighting features=-; External screw=Stainless steel; Fixing=Pole Head - Outreach; Gasket=Anti-aging silicone; General information=-; Glow Wire Test :=-; IPEA=ROAD = A3 + // LARGE AREAS = A4 + // CYCLOPEDONALS = A ++ // GREEN AREAS = A ++ // HISTORICAL CENTER = A6 +; Installationa and maintenance=-; LED Life Time (L80B05)=77000H; LED Maintenance=Not available; LED current.=0,7A; Lamp-=LED; Lifetime=L90B10 (Tq+25°C) = 100.000 h - L90B10 (Tq+50°C) = 75.000 h; Locking Hook=Integrated front handle; Lumen output (lm)=8300; Luminaire=LED Road Equipment; Materials=-; Maximum surface exposed to the wind=0,19M2; Maximum surface exposed to the wind :=0.19 m2; Minimum distance from the illuminated object=1M; Modello=GWR577330K; Mouting and installation=Pole Head - Outreach; Nominal flux (lm)=8100; Number of modules=3 (3x3 LED); Operating temperature :=-25 +50 °C; Operating temperature:=-25 +50 °C; Optic=WIDE; Optic :=Metallized polycarbonate reflector; Optic Maintenance=Not available; Optic and illuminating features=-; Overvoltage protection=DM 10KV / CM 10KV; Overvoltage resistance :=Common and dfferential mode: 10KV; Photobiological Risk Class=RG0; Rated frequency (Hz)=50 / 60; Shield type=4mm thick flat tempered glass; Standard Deviation Colour Matching=SDCM = 5; Standard-=EN 60598-2-3, EN 60598-1 IEC/TR 62778; Standards and approvals=-; Stocking temperature=-; Supply voltage=220 - 240 V; System power=79W; System power :=79 W @ 0.7A; Tilt adjustable=-20° ÷ +10° side bracket - -10° ÷ +20° pole head; Tilt-=-20° ÷ +10° side bracket - -10° ÷ +20° pole head; Tipo alimentatore=Constant Current Driver Led; Tipologia=Stand alone; Type of light source=LED - Not replaceable; Unified Glare Rating=G*3 - ULOR = 0; Unique digital code (Datamatrix)=Currently not present; Voltage-=220/240 V - 50/60 Hz - Stand alone; Weight (kg):=8; Wiring=Isolating switch
- GWR5714M - ROAD5 MEDI WIDE 4M 4000K 1,0A CL1 1-10V: Catalogue Range=ROAD [5]; Colour temperature=4000 K (CRI 70); Colour temperature:=4000 K (CRI 70); Descrizione=ROAD 5 MED.DIM.4M 4000K 1A O.W CL.I; EAN code=8011564873124; Electrocod=244C; LED LifeTime (L80B05)=120000H; LED current.=1A; Lamp-=LED; Lumen output (lm)=15360; Maximum surface exposed to the wind=0,19M2; Minimum distance from the illuminated object=1M; Modello=GWR5714M; No. Chorus modules=4 (4x3 LED); Nominal flux (lm)=19080; Number of modules=4 (4x3 LED); Operating temperature:=-25 +40 °C; Optic=W - ULOR: 0%; Overvoltage resistance=12 KV (Common and dfferential mode); Pilot current=1A; Power supply operation=Dimmable; System power=113W; Tilt adjustable=-20° ÷ +10° side bracket - -10° ÷ +20° pole head; Tipo alimentatore=Constant Current Driver Led; Tipologia=Dimmable; Voltage-=220/240 V - 50/60 Hz - Dimmable 1-10 V; Weight (kg)=8,4; Weight (kg):=8,4; Working temperature=-25 +40 °C
- GWR5773M - ROAD5 MEDI WIDE 3M 4000K 0,7A CL1 1-10V: Catalogue Range=ROAD [5]; Colour temperature=4000 K (CRI 70); Colour temperature:=4000 K (CRI 70); Descrizione=ROAD 5 MED.DIM.3M 4000K 700mA O.W CL.I; EAN code=8011564873384; Electrocod=244C; LED LifeTime (L80B05)=77000H; LED current.=0,7A; Lamp-=LED; Lumen output (lm)=7860; Maximum surface exposed to the wind=0,19M2; Minimum distance from the illuminated object=1M; Modello=GWR5773M; No. Chorus modules=3 (3x3 LED); Nominal flux (lm)=9360; Number of modules=3 (3x3 LED); Operating temperature:=-25 +50 °C; Optic=W - ULOR: 0%; Overvoltage resistance=12 KV (Common and dfferential mode); Pilot current=0,7A; Power supply operation=Dimmable; System power=79W; Tilt adjustable=-20° ÷ +10° side bracket - -10° ÷ +20° pole head; Tipo alimentatore=Constant Current Driver Led; Tipologia=Dimmable; Voltage-=220/240 V - 50/60 Hz - Dimmable 1-10 V; Weight (kg)=8; Weight (kg):=8; Working temperature=-25 +50 °C
- GWR5774 - ROAD 5 MED.S.AL.4M 4000K 700mA O.W CL.I: Catalogue Range=ROAD [5]; Colour temperature=4000 K (CRI 70); Colour temperature:=4000 K (CRI 70); Descrizione=ROAD 5 MED.S.AL.4M 4000K 700mA O.W CL.I; EAN code=8011564873391; Electrocod=244C; LED LifeTime (L80B05)=77000H; LED current.=0,7A; Lamp-=LED; Lumen output (lm)=10480; Maximum surface exposed to the wind=0,19M2; Minimum distance from the illuminated object=1M; Modello=GWR5774; No. Chorus modules=4 (4x3 LED); Nominal flux (lm)=12480; Number of modules=4 (4x3 LED); Operating temperature:=-25 +50 °C; Optic=W - ULOR: 0%; Overvoltage resistance=12 KV (Common and dfferential mode); Pilot current=0,7A; System power=106W; Tilt adjustable=-20° ÷ +10° side bracket - -10° ÷ +20° pole head; Tipo alimentatore=Constant Current Driver Led; Tipologia=Stand alone; Voltage-=220/240 V - 50/60 Hz - Stand alone; Weight (kg)=8,4; Weight (kg):=8,4; Working temperature=-25 +50 °C
- GWR5775B30K - ROAD5 MEDI WIDE 5M 3000K 0,7A CL1 BIREG: Body=Die-cast aluminium -; Catalogue Range=ROAD [5]; Classification:=-; Color Rendering Index=CRI-70; Colore=Graphite grey; Colour :=Powder coating; Colour temperature=3000K; Colour temperature:=3000 K (CRI>80); Context=Street and parking lighting; Control System=Bi-power with self-learning; DIN 18032-3 certification=-; Descrizione=GWR5775B30K - ROAD5 MEDI WIDE 5M 3000K 0,7A CL1 BIREG; Device with reduced surface temperature=-; Driver=Included; Driver Box=Built-in; Efficiency (lm/W)=102; Electrocod=244C; Eletrical and lighting features=-; External screw=Stainless steel; Fixing=Pole Head - Outreach; Gasket=Anti-aging silicone; General information=-; Glow Wire Test :=-; IPEA=ROAD = A // LARGE AREAS = A3 + // CYCLOPEDONALS = A // GREEN AREAS = A // HISTORICAL CENTER = A4 +; Installationa and maintenance=-; LED Life Time (L80B05)=77000H; LED Maintenance=Not available; LED current.=0,7A; Lamp-=LED; Lifetime=L90B10 (Tq+25°C) = 100.000 h - L90B10 (Tq+50°C) = 50.000 h; Locking Hook=Integrated front handle; Lumen output (lm)=13700; Luminaire=LED Road Equipment; Materials=-; Maximum surface exposed to the wind=0,19M2; Maximum surface exposed to the wind :=0.19 m2; Minimum distance from the illuminated object=1M; Modello=GWR5775B30K; Mouting and installation=Pole Head - Outreach; Nominal flux (lm)=13500; Number of modules=5 (5x3 LED); Operating temperature :=-25 +50 °C; Operating temperature:=-25 +50 °C; Optic=WIDE; Optic :=Metallized polycarbonate reflector; Optic Maintenance=Not available; Optic and illuminating features=-; Overvoltage protection=DM 10KV / CM 10KV; Overvoltage resistance :=Common and dfferential mode: 10KV; Photobiological Risk Class=RG0; Power supply operation=Bi power; Rated frequency (Hz)=50 / 60; Shield type=4mm thick flat tempered glass; Standard Deviation Colour Matching=SDCM = 5; Standard-=EN 60598-2-3, EN 60598-1 IEC/TR 62778; Standards and approvals=-; Stocking temperature=-; Supply voltage=220 - 240 V; System power=134W; System power :=134 W @ 0.7A; Tilt adjustable=-20° ÷ +10° side bracket - -10° ÷ +20° pole head; Tilt-=-20° ÷ +10° side bracket - -10° ÷ +20° pole head; Tipo alimentatore=Constant Current Driver Led; Tipologia=Bi power; Type of light source=LED - Not replaceable; Unified Glare Rating=G*3 - ULOR = 0; Unique digital code (Datamatrix)=Currently not present; Voltage-=220/240 V - 50/60 Hz - Bi-power with self-learning; Weight (kg):=8,8; Wiring=Isolating switch
- GWR5775B - ROAD 5 MED.BI-PO.5M 4000K 700mA O.W CL.I: Catalogue Range=ROAD [5]; Colour temperature=4000 K (CRI 70); Colour temperature:=4000 K (CRI 70); Descrizione=ROAD 5 MED.BI-PO.5M 4000K 700mA O.W CL.I; EAN code=8011564873438; Electrocod=244C; LED LifeTime (L80B05)=77000H; LED current.=0,7A; Lamp-=LED; Lumen output (lm)=13100; Maximum surface exposed to the wind=0,19M2; Minimum distance from the illuminated object=1M; Modello=GWR5775B; No. Chorus modules=5 (5x3 LED); Nominal flux (lm)=15600; Number of modules=5 (5x3 LED); Operating temperature:=-25 +50 °C; Optic=W - ULOR: 0%; Overvoltage resistance=12 KV (Common and dfferential mode); Pilot current=0,7A; Power supply operation=Bi power; System power=134W; Tilt adjustable=-20° ÷ +10° side bracket - -10° ÷ +20° pole head; Tipo alimentatore=Constant Current Driver Led; Tipologia=Bi power; Voltage-=220/240 V - 50/60 Hz - Bi-power with self-learning; Weight (kg)=8,8; Weight (kg):=8,8; Working temperature=-25 +50 °C
- GWR5713 - ROAD 5 MED.S.AL.3M 4000K 1A O.W CL.I: Catalogue Range=ROAD [5]; Colour temperature=4000 K (CRI 70); Colour temperature:=4000 K (CRI 70); Descrizione=ROAD 5 MED.S.AL.3M 4000K 1A O.W CL.I; EAN code=8011564873070; Electrocod=244C; LED LifeTime (L80B05)=120000H; LED current.=1A; Lamp-=LED; Lumen output (lm)=11520; Maximum surface exposed to the wind=0,19M2; Minimum distance from the illuminated object=1M; Modello=GWR5713; No. Chorus modules=3 (3x3 LED); Nominal flux (lm)=14310; Number of modules=3 (3x3 LED); Operating temperature:=-25 +40 °C; Optic=W - ULOR: 0%; Overvoltage resistance=12 KV (Common and dfferential mode); Pilot current=1A; System power=113W; Tilt adjustable=-20° ÷ +10° side bracket - -10° ÷ +20° pole head; Tipo alimentatore=Constant Current Driver Led; Tipologia=Stand alone; Voltage-=220/240 V - 50/60 Hz - Stand alone; Weight (kg)=8; Weight (kg):=8; Working temperature=-25 +40 °C
- GWR577530K - ROAD5 MEDI WIDE 5M 3000K 0,7A CL1: Body=Die-cast aluminium -; Catalogue Range=ROAD [5]; Classification:=-; Color Rendering Index=CRI-70; Colore=Graphite grey; Colour :=Powder coating; Colour temperature=3000K; Colour temperature:=3000 K (CRI>80); Context=Street and parking lighting; Control System=Stand alone; DIN 18032-3 certification=-; Descrizione=GWR577530K - ROAD5 MEDI WIDE 5M 3000K 0,7A CL1; Device with reduced surface temperature=-; Driver=Included; Driver Box=Built-in; Efficiency (lm/W)=104; Electrocod=244C; Eletrical and lighting features=-; External screw=Stainless steel; Fixing=Pole Head - Outreach; Gasket=Anti-aging silicone; General information=-; Glow Wire Test :=-; IPEA=ROAD = A // LARGE AREAS = A3 + // CYCLOPEDONALS = A // GREEN AREAS = A // HISTORICAL CENTER = A4 +; Installationa and maintenance=-; LED Life Time (L80B05)=77000H; LED Maintenance=Not available; LED current.=0,7A; Lamp-=LED; Lifetime=L90B10 (Tq+25°C) = 100.000 h - L90B10 (Tq+50°C) = 50.000 h; Locking Hook=Integrated front handle; Lumen output (lm)=13700; Luminaire=LED Road Equipment; Materials=-; Maximum surface exposed to the wind=0,19M2; Maximum surface exposed to the wind :=0.19 m2; Minimum distance from the illuminated object=1M; Modello=GWR577530K; Mouting and installation=Pole Head - Outreach; Nominal flux (lm)=13500; Number of modules=5 (5x3 LED); Operating temperature :=-25 +50 °C; Operating temperature:=-25 +50 °C; Optic=WIDE; Optic :=Metallized polycarbonate reflector; Optic Maintenance=Not available; Optic and illuminating features=-; Overvoltage protection=DM 10KV / CM 10KV; Overvoltage resistance :=Common and dfferential mode: 10KV; Photobiological Risk Class=RG0; Rated frequency (Hz)=50 / 60; Shield type=4mm thick flat tempered glass; Standard Deviation Colour Matching=SDCM = 5; Standard-=EN 60598-2-3, EN 60598-1 IEC/TR 62778; Standards and approvals=-; Stocking temperature=-; Supply voltage=220 - 240 V; System power=132W; System power :=132 W @ 0.7A; Tilt adjustable=-20° ÷ +10° side bracket - -10° ÷ +20° pole head; Tilt-=-20° ÷ +10° side bracket - -10° ÷ +20° pole head; Tipo alimentatore=Constant Current Driver Led; Tipologia=Stand alone; Type of light source=LED - Not replaceable; Unified Glare Rating=G*3 - ULOR = 0; Unique digital code (Datamatrix)=Currently not present; Voltage-=220/240 V - 50/60 Hz - Stand alone; Weight (kg):=8,8; Wiring=Isolating switch
- GWR5714B - ROAD5 MEDI WIDE 4M 4000K 1,0A CL1 BIREG: Catalogue Range=ROAD [5]; Colour temperature=4000 K (CRI 70); Colour temperature:=4000 K (CRI 70); Descrizione=ROAD 5 MED.BI-POW.4M 4000K 1A O.W CL.I; EAN code=8011564873117; Electrocod=244C; LED LifeTime (L80B05)=120000H; LED current.=1A; Lamp-=LED; Lumen output (lm)=15360; Maximum surface exposed to the wind=0,19M2; Minimum distance from the illuminated object=1M; Modello=GWR5714B; No. Chorus modules=4 (4x3 LED); Nominal flux (lm)=19080; Number of modules=4 (4x3 LED); Operating temperature:=-25 +40 °C; Optic=W - ULOR: 0%; Overvoltage resistance=12 KV (Common and dfferential mode); Pilot current=1A; Power supply operation=Bi power; System power=153W; Tilt adjustable=-20° ÷ +10° side bracket - -10° ÷ +20° pole head; Tipo alimentatore=Constant Current Driver Led; Tipologia=Bi power; Voltage-=220/240 V - 50/60 Hz - Bi-power with self-learning; Weight (kg)=8,4; Weight (kg):=8,4; Working temperature=-25 +40 °C

## geometry (parser evidence)
native form markers: Blend x2
no freeform markers — native parametric forms only
